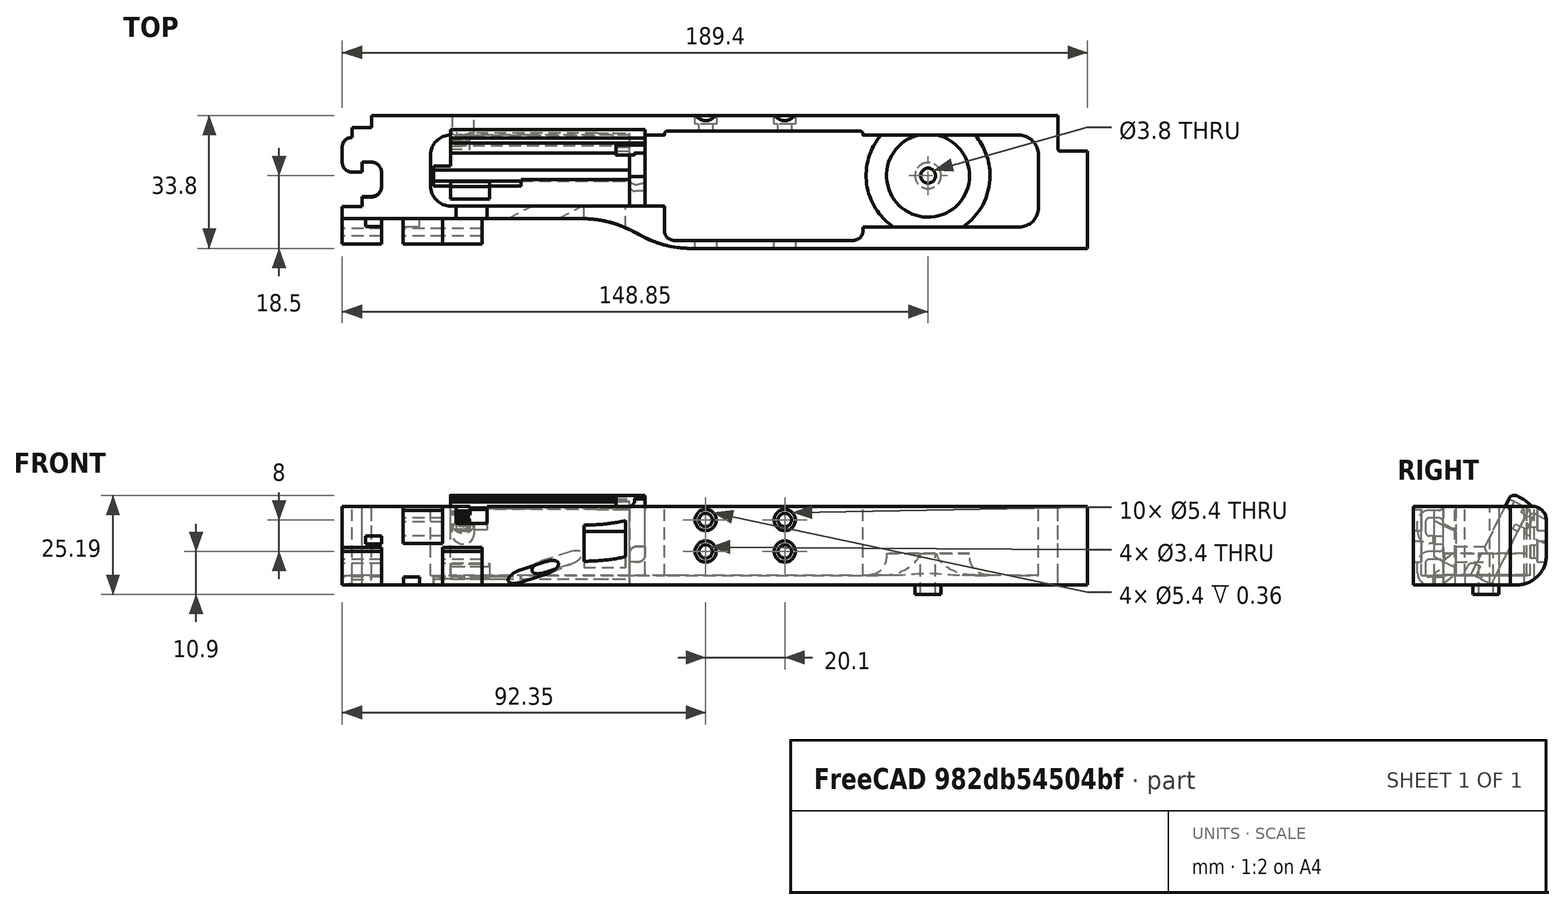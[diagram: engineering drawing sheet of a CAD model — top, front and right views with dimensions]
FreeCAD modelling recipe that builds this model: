
FCSTD DOCUMENT  (FreeCAD 0.19R0.19.2)
Label: v0_9995
License: All rights reserved
LicenseURL: http://en.wikipedia.org/wiki/All_rights_reserved
objects: Sketcher::SketchObject×44, Part::Extrusion×35, Part::MultiFuse×23, Part::Box×18, Part::Cut×15, Part::Fillet×13, App::MeasureDistance×10, Part::Cylinder×4, Part::Revolution×1, Mesh::Feature×1
note: 153 computed .brp shape members not serialized (recipe doc carries the construction recipe); baked Part::Feature solids carry a one-line shape summary decoded from their .brp

FEATURE [Sketcher::SketchObject] Sketch
  FullyConstrained = true
  sketch-geometry (36):
    g0: LineSegment StartX=0 StartY=0 StartZ=0 EndX=154.4 EndY=0 EndZ=0
    g1: LineSegment StartX=154.4 StartY=0 StartZ=0 EndX=154.4 EndY=-7.6 EndZ=0
    g2: LineSegment StartX=32.5209 StartY=-26.2 StartZ=0 EndX=-7.5 EndY=-26.2 EndZ=0
    g3-g7: Circle x5 (B-spline internal-alignment scaffolding for g8; pole/knot coordinates omitted)
    g8: BSplineCurve PolesCount=5 KnotsCount=3 Degree=3 IsPeriodic=0
    g9: GeomPoint X=61.85 Y=-33.8 Z=0
    g10: GeomPoint X=47.185 Y=-29.9 Z=0
    g11: GeomPoint X=32.5209 Y=-26.2 Z=0
    g12: Circle CenterX=121.35 CenterY=-14.3 CenterZ=0 NormalX=0 NormalY=0 NormalZ=1 AngleXU=0 Radius=3.25
    g13: LineSegment StartX=-7.5 StartY=-26.2 StartZ=0 EndX=-27.5 EndY=-26.2 EndZ=0
    g14: LineSegment StartX=-20 StartY=0 StartZ=0 EndX=0 EndY=0 EndZ=0
    g15: LineSegment StartX=-25 StartY=-3.1 StartZ=0 EndX=-20 EndY=-3.1 EndZ=0
    g16: LineSegment StartX=-25 StartY=-3.1 StartZ=0 EndX=-25 EndY=-5.6 EndZ=0
    g17: LineSegment StartX=-27.5 StartY=-8.1 StartZ=0 EndX=-27.5 EndY=-11.85 EndZ=0
    g18: ArcOfCircle CenterX=-25 CenterY=-8.1 CenterZ=0 NormalX=0 NormalY=0 NormalZ=1 AngleXU=0 Radius=2.5 StartAngle=1.5708 EndAngle=3.14159
    g19: LineSegment StartX=-25 StartY=-14.35 StartZ=0 EndX=-22.5 EndY=-14.35 EndZ=0
    g20: ArcOfCircle CenterX=-25 CenterY=-11.85 CenterZ=0 NormalX=0 NormalY=0 NormalZ=1 AngleXU=0 Radius=2.5 StartAngle=3.14159 EndAngle=4.71239
    g21: LineSegment StartX=-22.5 StartY=-14.35 StartZ=0 EndX=-22.5 EndY=-11.85 EndZ=0
    g22: LineSegment StartX=-22.5 StartY=-11.85 StartZ=0 EndX=-20 EndY=-11.85 EndZ=0
    g23: ArcOfCircle CenterX=-20 CenterY=-14.35 CenterZ=0 NormalX=0 NormalY=0 NormalZ=1 AngleXU=0 Radius=2.5 StartAngle=8e-16 EndAngle=1.5708
    g24: LineSegment StartX=-17.5 StartY=-14.35 StartZ=0 EndX=-17.5 EndY=-18.1 EndZ=0
    g25: ArcOfCircle CenterX=-20 CenterY=-18.1 CenterZ=0 NormalX=0 NormalY=0 NormalZ=1 AngleXU=0 Radius=2.5 StartAngle=4.71239 EndAngle=6.28319
    g26: LineSegment StartX=-22.5 StartY=-20.6 StartZ=0 EndX=-20 EndY=-20.6 EndZ=0
    g27: LineSegment StartX=-22.5 StartY=-20.6 StartZ=0 EndX=-22.5 EndY=-23.1 EndZ=0
    g28: LineSegment StartX=-27.5 StartY=-23.1 StartZ=0 EndX=-22.5 EndY=-23.1 EndZ=0
    g29: LineSegment StartX=-20 StartY=-3.1 StartZ=0 EndX=-20 EndY=0 EndZ=0
    g30: LineSegment StartX=-27.5 StartY=-23.1 StartZ=0 EndX=-27.5 EndY=-26.2 EndZ=0
    g31: LineSegment StartX=154.4 StartY=-7.6 StartZ=0 EndX=154.4 EndY=-8.6 EndZ=0
    g32: ArcOfCircle CenterX=154.9 CenterY=-8.6 CenterZ=0 NormalX=0 NormalY=0 NormalZ=1 AngleXU=0 Radius=0.5 StartAngle=3.14159 EndAngle=4.71239
    g33: LineSegment StartX=154.9 StartY=-9.1 StartZ=0 EndX=161.9 EndY=-9.1 EndZ=0
    g34: LineSegment StartX=161.9 StartY=-9.1 StartZ=0 EndX=161.9 EndY=-33.8 EndZ=0
    g35: LineSegment StartX=161.9 StartY=-33.8 StartZ=0 EndX=61.85 EndY=-33.8 EndZ=0
  constraints (72):
    c: PointOnObject(g0,g-2)
    c: Horizontal(g0)
    c: Distance(g0) = 154.4
    c: DistanceY(g-1,g0) = 0
    c: Vertical(g1)
    c: Distance(g1) = 7.6
    c: Coincident(g1,g0)
    c: Horizontal(g2)
    c: Block(g2)
    c: Weight(g3) = 1
    c: Coincident(g8,g2)
    c: InternalAlignment(g3-g7 -> g8) x5
    c: InternalAlignment(g9,g8)
    c: InternalAlignment(g10,g8)
    c: InternalAlignment(g11,g8)
    c: Block(g12)
    c: Coincident(g13,g2)
    c: Horizontal(g13)
    c: Distance(g13) = 20
    c: Horizontal(g14)
    c: Distance(g14) = 20
    c: Coincident(g14,g0)
    c: Horizontal(g15)
    c: Vertical(g16)
    c: Coincident(g16,g15)
    c: Vertical(g17)
    c: Coincident(g18,g16)
    c: Block(g18)
    c: Coincident(g17,g18)
    c: Horizontal(g19)
    c: Coincident(g20,g17)
    c: Block(g20)
    c: Block(g19)
    c: Vertical(g21)
    c: Coincident(g21,g19)
    c: Horizontal(g22)
    c: Coincident(g22,g21)
    c: Coincident(g23,g22)
    c: Vertical(g24)
    c: Block(g23)
    c: Coincident(g24,g23)
    c: Coincident(g25,g24)
    c: Block(g25)
    c: Horizontal(g26)
    c: Coincident(g26,g25)
    c: Vertical(g27)
    c: Coincident(g27,g26)
    c: Horizontal(g28)
    c: Coincident(g28,g27)
    c: Block(g15)
    c: Block(g28)
    c: Coincident(g29,g15)
    c: Coincident(g29,g14)
    c: Vertical(g29)
    c: Coincident(g30,g28)
    c: Coincident(g30,g13)
    c: Vertical(g30)
    c: Vertical(g31)
    c: Distance(g31) = 1
    c: Coincident(g31,g1)
    c: Coincident(g32,g31)
    c: Block(g32)
    c: Coincident(g33,g32)
    c: Horizontal(g33)
    c: Coincident(g34,g33)
    c: Vertical(g34)
    c: Block(g34)
    c: Coincident(g35,g34)
    c: Horizontal(g35)
    c: Block(g35)
    c: Coincident(g8,g35)
    c: Block(g8)
FEATURE [Part::Extrusion] Extrude  label="mainBodyBaseExtrude"
  Base = -> Sketch
  Dir = (0,0,1)
  DirMode = 2
  FaceMakerClass = Part::FaceMakerBullseye
  LengthFwd = 2.4
  LengthRev = 0
  Solid = true
  Symmetric = false
FEATURE [Sketcher::SketchObject] Sketch001
  FullyConstrained = true
  sketch-geometry (75):
    g0: ArcOfCircle CenterX=144.4 CenterY=-10 CenterZ=0 NormalX=0 NormalY=0 NormalZ=1 AngleXU=0 Radius=5 StartAngle=4.345e-13 EndAngle=1.5708
    g1: LineSegment StartX=32.5209 StartY=-26.2 StartZ=0 EndX=-7.49911 EndY=-26.2 EndZ=0
    g2: LineSegment StartX=0 StartY=0 StartZ=0 EndX=154.4 EndY=0 EndZ=0
    g3-g7: Circle x5 (B-spline internal-alignment scaffolding for g8; pole/knot coordinates omitted)
    g8: BSplineCurve PolesCount=5 KnotsCount=3 Degree=3 IsPeriodic=0
    g9: GeomPoint X=61.85 Y=-33.8 Z=0
    g10: GeomPoint X=47.1857 Y=-29.9 Z=0
    g11: GeomPoint X=32.5209 Y=-26.2 Z=0
    g12: LineSegment StartX=154.4 StartY=0 StartZ=0 EndX=154.4 EndY=-7.6 EndZ=0
    g13: LineSegment StartX=20 StartY=-5 StartZ=0 EndX=54.35 EndY=-5 EndZ=0
    g14: LineSegment StartX=104.85 StartY=-5 StartZ=0 EndX=144.4 EndY=-5 EndZ=0
    g15: LineSegment StartX=54.35 StartY=-23 StartZ=0 EndX=20 EndY=-23 EndZ=0
    g16: LineSegment StartX=-27.4991 StartY=-26.2 StartZ=0 EndX=-7.49911 EndY=-26.2 EndZ=0
    g17: LineSegment StartX=-20 StartY=0 StartZ=0 EndX=0 EndY=0 EndZ=0
    g18: LineSegment StartX=-27.4991 StartY=-23.2 StartZ=0 EndX=-22.5 EndY=-23.2 EndZ=0
    g19: LineSegment StartX=-22.5 StartY=-20.7 StartZ=0 EndX=-22.5 EndY=-23.2 EndZ=0
    g20: LineSegment StartX=-22.5 StartY=-20.7 StartZ=0 EndX=-20 EndY=-20.7 EndZ=0
    g21: ArcOfCircle CenterX=-20 CenterY=-18.2 CenterZ=0 NormalX=0 NormalY=0 NormalZ=1 AngleXU=0 Radius=2.5 StartAngle=4.71239 EndAngle=6.28319
    g22: LineSegment StartX=-17.5 StartY=-14.4 StartZ=0 EndX=-17.5 EndY=-18.2 EndZ=0
    g23: ArcOfCircle CenterX=-20 CenterY=-14.4 CenterZ=0 NormalX=0 NormalY=0 NormalZ=1 AngleXU=0 Radius=2.5 StartAngle=9e-16 EndAngle=1.5708
    g24: LineSegment StartX=-22.5 StartY=-11.9 StartZ=0 EndX=-20 EndY=-11.9 EndZ=0
    g25: LineSegment StartX=-22.5 StartY=-14.4 StartZ=0 EndX=-22.5 EndY=-11.9 EndZ=0
    g26: LineSegment StartX=-25 StartY=-14.4 StartZ=0 EndX=-22.5 EndY=-14.4 EndZ=0
    g27: ArcOfCircle CenterX=-25 CenterY=-11.9 CenterZ=0 NormalX=0 NormalY=0 NormalZ=1 AngleXU=0 Radius=2.5 StartAngle=3.14159 EndAngle=4.71239
    g28: LineSegment StartX=-27.5 StartY=-8.1 StartZ=0 EndX=-27.5 EndY=-11.9 EndZ=0
    g29: ArcOfCircle CenterX=-25 CenterY=-8.1 CenterZ=0 NormalX=0 NormalY=0 NormalZ=1 AngleXU=0 Radius=2.5 StartAngle=1.5708 EndAngle=3.14159
    g30: LineSegment StartX=-25 StartY=-3.1 StartZ=0 EndX=-25 EndY=-5.6 EndZ=0
    g31: LineSegment StartX=-20 StartY=-3.1 StartZ=0 EndX=-25 EndY=-3.1 EndZ=0
    g32: LineSegment StartX=-20 StartY=0 StartZ=0 EndX=-20 EndY=-3.1 EndZ=0
    g33: LineSegment StartX=-27.4991 StartY=-26.2 StartZ=0 EndX=-27.4991 EndY=-23.2 EndZ=0
    g34: LineSegment StartX=4.09e-14 StartY=-5 StartZ=0 EndX=20 EndY=-5 EndZ=0
    g35: ArcOfCircle CenterX=7.1e-15 CenterY=-18 CenterZ=0 NormalX=0 NormalY=0 NormalZ=1 AngleXU=0 Radius=5 StartAngle=3.14159 EndAngle=4.71239
    g36: ArcOfCircle CenterX=4.26e-14 CenterY=-10 CenterZ=0 NormalX=0 NormalY=0 NormalZ=1 AngleXU=0 Radius=5 StartAngle=1.5708 EndAngle=3.14159
    g37: LineSegment StartX=-5 StartY=-18 StartZ=0 EndX=-5 EndY=-10 EndZ=0
    g38: LineSegment StartX=6.2e-15 StartY=-23 StartZ=0 EndX=20 EndY=-23 EndZ=0
    g39: LineSegment StartX=154.4 StartY=-7.6 StartZ=0 EndX=154.4 EndY=-8.6 EndZ=0
    g40: LineSegment StartX=154.9 StartY=-9.1 StartZ=0 EndX=161.9 EndY=-9.1 EndZ=0
    g41: ArcOfCircle CenterX=154.9 CenterY=-8.6 CenterZ=0 NormalX=0 NormalY=0 NormalZ=1 AngleXU=0 Radius=0.5 StartAngle=3.14159 EndAngle=4.71299
    g42: LineSegment StartX=104.85 StartY=-28.3916 StartZ=0 EndX=144.408 EndY=-28.3916 EndZ=0
    g43: LineSegment StartX=149.4 StartY=-10 StartZ=0 EndX=149.4 EndY=-23.4 EndZ=0
    g44: ArcOfCircle CenterX=144.408 CenterY=-23.4 CenterZ=0 NormalX=0 NormalY=0 NormalZ=1 AngleXU=0 Radius=4.99164 StartAngle=4.71239 EndAngle=6.28319
    g45: LineSegment StartX=104.85 StartY=-28.3916 StartZ=0 EndX=104.85 EndY=-28.7833 EndZ=0
    g46: LineSegment StartX=54.35 StartY=-28.7916 StartZ=0 EndX=54.35 EndY=-23 EndZ=0
    g47: LineSegment StartX=161.9 StartY=-33.8 StartZ=0 EndX=161.9 EndY=-9.1 EndZ=0
    g48: LineSegment StartX=61.85 StartY=-33.8 StartZ=0 EndX=161.9 EndY=-33.8 EndZ=0
    g49: Circle CenterX=54.35 CenterY=-28.7916 CenterZ=0 NormalX=0 NormalY=0 NormalZ=1 AngleXU=0 Radius=1
    g50: Circle CenterX=54.35 CenterY=-31.7916 CenterZ=0 NormalX=0 NormalY=0 NormalZ=1 AngleXU=0 Radius=1
    g51: Circle CenterX=57.35 CenterY=-31.7916 CenterZ=0 NormalX=0 NormalY=0 NormalZ=1 AngleXU=0 Radius=1
    g52: BSplineCurve PolesCount=3 KnotsCount=2 Degree=2 IsPeriodic=0
    g53: GeomPoint X=54.35 Y=-28.7916 Z=0
    g54: GeomPoint X=57.35 Y=-31.7916 Z=0
    g55: Circle CenterX=104.85 CenterY=-28.7833 CenterZ=0 NormalX=0 NormalY=0 NormalZ=1 AngleXU=0 Radius=1
    g56: Circle CenterX=104.85 CenterY=-31.7916 CenterZ=0 NormalX=0 NormalY=0 NormalZ=1 AngleXU=0 Radius=1
    g57: Circle CenterX=101.85 CenterY=-31.7916 CenterZ=0 NormalX=0 NormalY=0 NormalZ=1 AngleXU=0 Radius=1
    g58: BSplineCurve PolesCount=3 KnotsCount=2 Degree=2 IsPeriodic=0
    g59: GeomPoint X=104.85 Y=-28.7833 Z=0
    g60: GeomPoint X=101.85 Y=-31.7916 Z=0
    g61: LineSegment StartX=57.35 StartY=-31.7916 StartZ=0 EndX=101.85 EndY=-31.7916 EndZ=0
    g62: Circle CenterX=54.35 CenterY=-5 CenterZ=0 NormalX=0 NormalY=0 NormalZ=1 AngleXU=0 Radius=1
    g63: Circle CenterX=54.35 CenterY=-4 CenterZ=0 NormalX=0 NormalY=0 NormalZ=1 AngleXU=0 Radius=1
    g64: Circle CenterX=55.15 CenterY=-4 CenterZ=0 NormalX=0 NormalY=0 NormalZ=1 AngleXU=0 Radius=1
    g65: BSplineCurve PolesCount=3 KnotsCount=2 Degree=2 IsPeriodic=0
    g66: GeomPoint X=54.35 Y=-5 Z=0
    g67: GeomPoint X=55.15 Y=-4 Z=0
    g68: Circle CenterX=104.85 CenterY=-5 CenterZ=0 NormalX=0 NormalY=0 NormalZ=1 AngleXU=0 Radius=1
    g69: Circle CenterX=104.85 CenterY=-4 CenterZ=0 NormalX=0 NormalY=0 NormalZ=1 AngleXU=0 Radius=1
    g70: Circle CenterX=104.05 CenterY=-4 CenterZ=0 NormalX=0 NormalY=0 NormalZ=1 AngleXU=0 Radius=1
    g71: BSplineCurve PolesCount=3 KnotsCount=2 Degree=2 IsPeriodic=0
    g72: GeomPoint X=104.85 Y=-5 Z=0
    g73: GeomPoint X=104.05 Y=-4 Z=0
    g74: LineSegment StartX=104.05 StartY=-4 StartZ=0 EndX=55.15 EndY=-4 EndZ=0
  constraints (156):
    c: PointOnObject(g2,g-2)
    c: DistanceY(g-1,g2) = 0
    c: Block(g0)
    c: Horizontal(g1)
    c: Distance(g1) = 40.02
    c: Horizontal(g2)
    c: Block(g2)
    c: Weight(g3) = 1
    c: Equal(g3, g4-g7) x4
    c: Coincident(g8,g1)
    c: InternalAlignment(g3-g7 -> g8) x5
    c: InternalAlignment(g9,g8)
    c: InternalAlignment(g10,g8)
    c: InternalAlignment(g11,g8)
    c: Vertical(g12)
    c: Coincident(g12,g2)
    c: Distance(g12) = 7.6
    c: Block(g12)
    c: Horizontal(g13)
    c: Coincident(g14,g0)
    c: Horizontal(g14)
    c: Horizontal(g15)
    c: Horizontal(g16)
    c: Distance(g16) = 20
    c: Coincident(g1,g16)
    c: Horizontal(g17)
    c: Distance(g17) = 20
    c: Coincident(g17,g2)
    c: Horizontal(g31)
    c: Vertical(g30)
    c: Coincident(g29,g30)
    c: Vertical(g28)
    c: Block(g29)
    c: Coincident(g27,g28)
    c: Block(g27)
    c: Horizontal(g26)
    c: Coincident(g26,g27)
    c: Vertical(g25)
    c: Coincident(g25,g26)
    c: Horizontal(g24)
    c: Coincident(g23,g24)
    c: Block(g23)
    c: Vertical(g22)
    c: Coincident(g21,g22)
    c: Block(g21)
    c: Horizontal(g20)
    c: Coincident(g20,g21)
    c: Vertical(g19)
    c: Coincident(g19,g20)
    c: Horizontal(g18)
    c: Coincident(g18,g19)
    c: Coincident(g32,g17)
    c: Coincident(g32,g31)
    c: Vertical(g32)
    c: Coincident(g33,g16)
    c: Coincident(g33,g18)
    c: Vertical(g33)
    c: Block(g33)
    c: Block(g18)
    c: Block(g22)
    c: Block(g26)
    c: Block(g25)
    c: Block(g24)
    c: Block(g28)
    c: Block(g31)
    c: Block(g30)
    c: Horizontal(g34)
    c: Distance(g34) = 20
    c: Block(g35)
    c: Block(g36)
    c: Coincident(g37,g35)
    c: Coincident(g37,g36)
    c: Vertical(g37)
    c: Coincident(g38,g35)
    c: Coincident(g38,g15)
    c: Horizontal(g38)
    c: Block(g38)
    c: Block(g34)
    c: Block(g13)
    c: Vertical(g39)
    c: Distance(g39) = 1
    c: Coincident(g39,g12)
    c: Horizontal(g40)
    c: Coincident(g41,g39)
    c: Coincident(g41,g40)
    c: Block(g39)
    c: Block(g41)
    c: Horizontal(g42)
    c: Vertical(g43)
    c: Distance(g43) = 13.4
    c: Coincident(g43,g0)
    c: Block(g42)
    c: Block(g43)
    c: Coincident(g44,g43)
    c: Coincident(g44,g42)
    c: Block(g44)
    c: Distance(g15) = 34.35
    c: Coincident(g45,g42)
    c: Vertical(g45)
    c: Coincident(g46,g15)
    c: Vertical(g46)
    c: Coincident(g47,g40)
    c: Vertical(g47)
    c: Block(g47)
    c: Coincident(g48,g47)
    c: Horizontal(g48)
    c: Block(g48)
    c: Coincident(g8,g48)
    c: Block(g8)
    c: Coincident(g52,g46)
    c: Weight(g49) = 1
    c: Equal(g49,g50)
    c: Equal(g49,g51)
    c: InternalAlignment(g49,g52)
    c: InternalAlignment(g50,g52)
    c: InternalAlignment(g51,g52)
    c: InternalAlignment(g53,g52)
    c: InternalAlignment(g54,g52)
    c: Coincident(g58,g45)
    c: Weight(g55) = 1
    c: Equal(g55,g56)
    c: Equal(g55,g57)
    c: InternalAlignment(g55,g58)
    c: InternalAlignment(g56,g58)
    c: InternalAlignment(g57,g58)
    c: InternalAlignment(g59,g58)
    c: InternalAlignment(g60,g58)
    c: Block(g58)
    c: Block(g52)
    c: Coincident(g61,g52)
    c: Coincident(g61,g58)
    c: Horizontal(g61)
    c: Block(g14)
    c: Coincident(g65,g13)
    c: Weight(g62) = 1
    c: Equal(g62,g63)
    c: Equal(g62,g64)
    c: InternalAlignment(g62,g65)
    c: InternalAlignment(g63,g65)
    c: InternalAlignment(g64,g65)
    c: InternalAlignment(g66,g65)
    c: InternalAlignment(g67,g65)
    c: Block(g65)
    c: Coincident(g71,g14)
    c: Weight(g68) = 1
    c: Equal(g68,g69)
    c: Equal(g68,g70)
    c: InternalAlignment(g68,g71)
    c: InternalAlignment(g69,g71)
    c: InternalAlignment(g70,g71)
    c: InternalAlignment(g72,g71)
    c: InternalAlignment(g73,g71)
    c: Block(g71)
    c: Coincident(g74,g71)
    c: Coincident(g74,g65)
    c: Horizontal(g74)
FEATURE [Sketcher::SketchObject] Sketch005
  FullyConstrained = true
  Placement = pos=(0,0,0) rot=(1,0,0;1.5708rad)
  sketch-geometry (4):
    g0: Circle CenterX=84.95 CenterY=16.5 CenterZ=0 NormalX=0 NormalY=0 NormalZ=1 AngleXU=0 Radius=1.7
    g1: Circle CenterX=84.95 CenterY=8.5 CenterZ=0 NormalX=0 NormalY=0 NormalZ=1 AngleXU=0 Radius=1.7
    g2: Circle CenterX=64.85 CenterY=8.5 CenterZ=0 NormalX=0 NormalY=0 NormalZ=1 AngleXU=0 Radius=1.7
    g3: Circle CenterX=64.85 CenterY=16.5 CenterZ=0 NormalX=0 NormalY=0 NormalZ=1 AngleXU=0 Radius=1.7
  constraints (4):
    c: Block(g0)
    c: Block(g1)
    c: Block(g2)
    c: Block(g3)
FEATURE [Part::Extrusion] Extrude004  label="removeFromMainBodyToCreateScrewHolesForSolenoidExtrude004"
  Base = -> Sketch005
  Dir = (0,-1,1.1e-15)
  DirMode = 2
  FaceMakerClass = Part::FaceMakerBullseye
  LengthFwd = 10
  LengthRev = 0
  Solid = true
  Symmetric = false
FEATURE [Sketcher::SketchObject] Sketch004
  FullyConstrained = true
  Placement = pos=(0,0,0) rot=(1,0,0;1.5708rad)
  sketch-geometry (12):
    g0: LineSegment StartX=15.75 StartY=2.5 StartZ=0 EndX=15.75 EndY=0 EndZ=0
    g1: Circle CenterX=15.75 CenterY=2.5 CenterZ=0 NormalX=0 NormalY=0 NormalZ=1 AngleXU=0 Radius=1
    g2: Circle CenterX=10.55 CenterY=2.5 CenterZ=0 NormalX=0 NormalY=0 NormalZ=1 AngleXU=0 Radius=1
    g3: Circle CenterX=10.55 CenterY=8 CenterZ=0 NormalX=0 NormalY=0 NormalZ=1 AngleXU=0 Radius=1
    g4: BSplineCurve PolesCount=3 KnotsCount=2 Degree=2 IsPeriodic=0
    g5: GeomPoint X=15.75 Y=2.5 Z=0
    g6: GeomPoint X=10.55 Y=8 Z=0
    g7: LineSegment StartX=1.9 StartY=8 StartZ=0 EndX=10.55 EndY=8 EndZ=0
    g8: LineSegment StartX=1.9 StartY=-2.4 StartZ=0 EndX=1.9 EndY=8 EndZ=0
    g9: LineSegment StartX=3.30092 StartY=-2.4 StartZ=0 EndX=3.30092 EndY=0 EndZ=0
    g10: LineSegment StartX=15.75 StartY=0 StartZ=0 EndX=3.30092 EndY=0 EndZ=0
    g11: LineSegment StartX=3.30092 StartY=-2.4 StartZ=0 EndX=1.9 EndY=-2.4 EndZ=0
  constraints (26):
    c: Vertical(g0)
    c: Distance(g0) = 2.5
    c: Coincident(g4,g0)
    c: Weight(g1) = 1
    c: Equal(g1,g2)
    c: Equal(g1,g3)
    c: InternalAlignment(g1,g4)
    c: InternalAlignment(g2,g4)
    c: InternalAlignment(g3,g4)
    c: InternalAlignment(g5,g4)
    c: InternalAlignment(g6,g4)
    c: Block(g4)
    c: Coincident(g7,g4)
    c: Horizontal(g7)
    c: Vertical(g8)
    c: Coincident(g8,g7)
    c: Block(g8)
    c: Vertical(g9)
    c: Coincident(g10,g0)
    c: PointOnObject(g10,g-1)
    c: Horizontal(g10)
    c: Coincident(g10,g9)
    c: Block(g9)
    c: Coincident(g11,g9)
    c: Coincident(g11,g8)
    c: Horizontal(g11)
FEATURE [Sketcher::SketchObject] Sketch007
  FullyConstrained = true
  Placement = pos=(0,-14.3,2.37) rot=(-1,0,0;2.03453rad)
  sketch-geometry (6):
    g0: LineSegment StartX=0 StartY=0 StartZ=0 EndX=45.5 EndY=0 EndZ=0
    g1: LineSegment StartX=0 StartY=0 StartZ=0 EndX=0 EndY=-21.2 EndZ=0
    g2: LineSegment StartX=45.5 StartY=0 StartZ=0 EndX=49.5 EndY=0 EndZ=0
    g3: LineSegment StartX=49.5 StartY=0 StartZ=0 EndX=49.5 EndY=-21.2 EndZ=0
    g4: LineSegment StartX=49.5 StartY=-21.2 StartZ=0 EndX=0 EndY=-21.2 EndZ=0
    g5: Circle CenterX=3.25 CenterY=-18.05 CenterZ=0 NormalX=0 NormalY=0 NormalZ=1 AngleXU=0 Radius=1.6
  constraints (15):
    c: Coincident(g0,g-1)
    c: Horizontal(g0)
    c: Distance(g0) = 45.5
    c: Coincident(g1,g0)
    c: Vertical(g1)
    c: Horizontal(g2)
    c: Distance(g2) = 4
    c: Coincident(g2,g0)
    c: Coincident(g3,g2)
    c: Vertical(g3)
    c: Block(g3)
    c: Coincident(g4,g3)
    c: Horizontal(g4)
    c: Coincident(g4,g1)
    c: Block(g5)
FEATURE [Part::Extrusion] Extrude005  label="solenoidDriverHolderExtrude005"
  Base = -> Sketch007
  Dir = (0,0.894389,-0.447291)
  DirMode = 2
  FaceMakerClass = Part::FaceMakerBullseye
  LengthFwd = 10
  LengthRev = 0
  Placement = pos=(0,0,-2) rot=(0,0,1;0rad)
  Solid = true
  Symmetric = false
FEATURE [Sketcher::SketchObject] Sketch008
  FullyConstrained = false
  Placement = pos=(0,-4.3,-2.6) rot=(-1,0,0;2.03453rad)
  sketch-geometry (1):
    g0: Circle CenterX=42.25 CenterY=-3.15 CenterZ=0 NormalX=0 NormalY=0 NormalZ=1 AngleXU=0 Radius=4.5
FEATURE [Sketcher::SketchObject] Sketch009
  FullyConstrained = true
  Placement = pos=(0,-4.3,-2.6) rot=(-1,0,0;2.03453rad)
  sketch-geometry (1):
    g0: Circle CenterX=3.25 CenterY=-18.0217 CenterZ=0 NormalX=0 NormalY=0 NormalZ=1 AngleXU=0 Radius=2.8
  constraints (1):
    c: Block(g0)
FEATURE [Sketcher::SketchObject] Sketch010
  FullyConstrained = true
  Placement = pos=(0,-14.3,2.37) rot=(-1,0,0;2.03453rad)
  sketch-geometry (1):
    g0: Circle CenterX=3.25 CenterY=-18.05 CenterZ=0 NormalX=0 NormalY=0 NormalZ=1 AngleXU=0 Radius=1.6
  constraints (1):
    c: Block(g0)
FEATURE [Part::Extrusion] Extrude008  label="removeFromScrewHole3"
  Base = -> Sketch010
  Dir = (0,0.894389,-0.447291)
  DirMode = 2
  FaceMakerClass = Part::FaceMakerBullseye
  LengthFwd = -25
  LengthRev = 0
  Placement = pos=(0,4,-4) rot=(0,0,1;0rad)
  Solid = true
  Symmetric = false
FEATURE [Sketcher::SketchObject] Sketch011
  FullyConstrained = true
  Placement = pos=(0,-14.3,2.37) rot=(-1,0,0;2.03453rad)
  sketch-geometry (4):
    g0: LineSegment StartX=49.5 StartY=-21.2 StartZ=0 EndX=49.5 EndY=-22.8 EndZ=0
    g1: LineSegment StartX=49.5 StartY=-22.8 StartZ=0 EndX=0.002238 EndY=-22.8 EndZ=0
    g2: LineSegment StartX=0.002238 StartY=-21.2 StartZ=0 EndX=0.002238 EndY=-22.8 EndZ=0
    g3: LineSegment StartX=49.5 StartY=-21.2 StartZ=0 EndX=0.002238 EndY=-21.2 EndZ=0
  constraints (10):
    c: Vertical(g0)
    c: Distance(g0) = 1.6
    c: Coincident(g1,g0)
    c: Horizontal(g1)
    c: Vertical(g2)
    c: Coincident(g2,g1)
    c: Coincident(g3,g0)
    c: Coincident(g3,g2)
    c: Horizontal(g3)
    c: Block(g3)
FEATURE [Part::Extrusion] Extrude009  label="solenoidDriverTopLipFront"
  Base = -> Sketch011
  Dir = (0,0.894389,-0.447291)
  DirMode = 2
  FaceMakerClass = Part::FaceMakerBullseye
  LengthFwd = -2
  LengthRev = 0
  Placement = pos=(0,-2.9,-0.35) rot=(0,0,1;0rad)
  Solid = true
  Symmetric = false
FEATURE [Sketcher::SketchObject] Sketch012
  FullyConstrained = true
  Placement = pos=(0,-14.3,2.37) rot=(-1,0,0;2.03453rad)
  sketch-geometry (4):
    g0: LineSegment StartX=49.5 StartY=-21.2 StartZ=0 EndX=49.5 EndY=-22.8 EndZ=0
    g1: LineSegment StartX=49.5 StartY=-22.8 StartZ=0 EndX=0.002238 EndY=-22.8 EndZ=0
    g2: LineSegment StartX=0.002238 StartY=-21.2 StartZ=0 EndX=0.002238 EndY=-22.8 EndZ=0
    g3: LineSegment StartX=49.5 StartY=-21.2 StartZ=0 EndX=0.002238 EndY=-21.2 EndZ=0
  constraints (10):
    c: Vertical(g0)
    c: Distance(g0) = 1.6
    c: Coincident(g1,g0)
    c: Horizontal(g1)
    c: Vertical(g2)
    c: Coincident(g2,g1)
    c: Coincident(g3,g0)
    c: Coincident(g3,g2)
    c: Horizontal(g3)
    c: Block(g3)
FEATURE [Part::Extrusion] Extrude010  label="solenoidDriverTopLipLowerExtrude010"
  Base = -> Sketch012
  Dir = (0,0.894389,-0.447291)
  DirMode = 2
  FaceMakerClass = Part::FaceMakerBullseye
  LengthFwd = 5.05
  LengthRev = 0
  Solid = true
  Symmetric = false
FEATURE [Sketcher::SketchObject] Sketch015
  FullyConstrained = true
  Placement = pos=(0,-14.3,2.37) rot=(-1,0,0;2.03453rad)
  sketch-geometry (4):
    g0: LineSegment StartX=0 StartY=1.5 StartZ=0 EndX=0 EndY=0 EndZ=0
    g1: LineSegment StartX=0 StartY=1.5 StartZ=0 EndX=5 EndY=1.5 EndZ=0
    g2: LineSegment StartX=5 StartY=1.5 StartZ=0 EndX=5 EndY=0 EndZ=0
    g3: LineSegment StartX=0 StartY=0 StartZ=0 EndX=5 EndY=0 EndZ=0
  constraints (13):
    c: Vertical(g0)
    c: Distance(g0) = 1.5
    c: Horizontal(g1)
    c: Distance(g1) = 5
    c: Coincident(g1,g0)
    c: Vertical(g2)
    c: Distance(g2) = 1.5
    c: Coincident(g2,g1)
    c: Block(g1)
    c: Block(g2)
    c: Block(g0)
    c: Coincident(g3,g0)
    c: Coincident(g3,g2)
FEATURE [Part::Extrusion] Extrude013  label="solenoidDriverBottomLipTopExtrude012"
  Base = -> Sketch015
  Dir = (0,0.894389,-0.447291)
  DirMode = 2
  FaceMakerClass = Part::FaceMakerBullseye
  LengthFwd = -6.5
  LengthRev = 0
  Placement = pos=(0,-14.15,19.65) rot=(1,0,0;1.5708rad)
  Solid = true
  Symmetric = false
FEATURE [Sketcher::SketchObject] Sketch016
  FullyConstrained = true
  Placement = pos=(0,0,0) rot=(1,0,0;1.5708rad)
  sketch-geometry (4):
    g0: Circle CenterX=84.15 CenterY=16.5 CenterZ=0 NormalX=0 NormalY=0 NormalZ=1 AngleXU=0 Radius=2.7
    g1: Circle CenterX=64.05 CenterY=16.5 CenterZ=0 NormalX=0 NormalY=0 NormalZ=1 AngleXU=0 Radius=2.7
    g2: Circle CenterX=64.05 CenterY=8.5 CenterZ=0 NormalX=0 NormalY=0 NormalZ=1 AngleXU=0 Radius=2.7
    g3: Circle CenterX=84.15 CenterY=8.5 CenterZ=0 NormalX=0 NormalY=0 NormalZ=1 AngleXU=0 Radius=2.7
  constraints (4):
    c: Block(g0)
    c: Block(g1)
    c: Block(g3)
    c: Block(g2)
FEATURE [Part::Extrusion] Extrude014  label="removeFromMainBodyToCreateScrewHoleCounterSinks"
  Base = -> Sketch016
  Dir = (0,-1,1.1e-15)
  DirMode = 2
  FaceMakerClass = Part::FaceMakerBullseye
  LengthFwd = 1.9
  LengthRev = 0
  Placement = pos=(0.8,-0.36,0) rot=(0,0,1;0rad)
  Solid = true
  Symmetric = false
FEATURE [Part::Extrusion] Extrude015  label="removeFromScrewHole2Extrude007"
  Base = -> Sketch009
  Dir = (0,0.894389,-0.447291)
  DirMode = 2
  FaceMakerClass = Part::FaceMakerBullseye
  LengthFwd = 10
  LengthRev = 0
  Placement = pos=(0,-8,2) rot=(0,0,1;0rad)
  Solid = true
  Symmetric = false
FEATURE [Sketcher::SketchObject] Sketch017
  FullyConstrained = true
  Placement = pos=(0,-14.3,2.37) rot=(-1,0,0;2.03453rad)
  sketch-geometry (4):
    g0: LineSegment StartX=0 StartY=1.5 StartZ=0 EndX=0 EndY=0 EndZ=0
    g1: LineSegment StartX=0 StartY=1.5 StartZ=0 EndX=5 EndY=1.5 EndZ=0
    g2: LineSegment StartX=5 StartY=1.5 StartZ=0 EndX=5 EndY=0 EndZ=0
    g3: LineSegment StartX=0 StartY=0 StartZ=0 EndX=5 EndY=0 EndZ=0
  constraints (13):
    c: Vertical(g0)
    c: Distance(g0) = 1.5
    c: Horizontal(g1)
    c: Distance(g1) = 5
    c: Coincident(g1,g0)
    c: Vertical(g2)
    c: Distance(g2) = 1.5
    c: Coincident(g2,g1)
    c: Block(g1)
    c: Block(g2)
    c: Block(g0)
    c: Coincident(g3,g0)
    c: Coincident(g3,g2)
FEATURE [Part::Extrusion] Extrude016  label="solenoidDriverBottomLipTopExtrude013"
  Base = -> Sketch017
  Dir = (0,0.894389,-0.447291)
  DirMode = 2
  FaceMakerClass = Part::FaceMakerBullseye
  LengthFwd = -6.5
  LengthRev = 0
  Placement = pos=(0,-15.45,20.3) rot=(1,0,0;1.5708rad)
  Solid = true
  Symmetric = false
FEATURE [Part::Fillet] Fillet005  label="solenoidDriverBottomLipTopFillet005"
  Base = -> Extrude016
  Edges = 1 edges r=1.4: [Edge6]
FEATURE [Sketcher::SketchObject] Sketch018
  FullyConstrained = true
  Placement = pos=(38.5,-14.3,2.37) rot=(-1,0,0;2.03453rad)
  sketch-geometry (4):
    g0: LineSegment StartX=11 StartY=0 StartZ=0 EndX=11 EndY=1.5 EndZ=0
    g1: LineSegment StartX=11 StartY=0 StartZ=0 EndX=3.6 EndY=0 EndZ=0
    g2: LineSegment StartX=3.6 StartY=0 StartZ=0 EndX=3.6 EndY=1.5 EndZ=0
    g3: LineSegment StartX=11 StartY=1.5 StartZ=0 EndX=3.6 EndY=1.5 EndZ=0
  constraints (12):
    c: PointOnObject(g0,g-1)
    c: Vertical(g0)
    c: Distance(g0) = 1.5
    c: Horizontal(g1)
    c: Distance(g1) = 7.4
    c: Coincident(g1,g0)
    c: Block(g0)
    c: Coincident(g2,g1)
    c: Vertical(g2)
    c: Coincident(g3,g0)
    c: Horizontal(g3)
    c: Coincident(g2,g3)
FEATURE [Part::Extrusion] Extrude017
  Base = -> Sketch018
  Dir = (0,0.894389,-0.447291)
  DirMode = 2
  FaceMakerClass = Part::FaceMakerBullseye
  LengthFwd = 4
  LengthRev = 0
  Placement = pos=(0,-8.212,34.025) rot=(1,0,0;1.5708rad)
  Solid = true
  Symmetric = false
FEATURE [Sketcher::SketchObject] Sketch019
  FullyConstrained = true
  Placement = pos=(0,0,0) rot=(1,0,0;1.5708rad)
  sketch-geometry (4):
    g0: Circle CenterX=84.95 CenterY=8.5 CenterZ=0 NormalX=0 NormalY=0 NormalZ=1 AngleXU=0 Radius=2.7
    g1: Circle CenterX=64.85 CenterY=8.5 CenterZ=0 NormalX=0 NormalY=0 NormalZ=1 AngleXU=0 Radius=2.7
    g2: Circle CenterX=64.85 CenterY=16.5 CenterZ=0 NormalX=0 NormalY=0 NormalZ=1 AngleXU=0 Radius=2.7
    g3: Circle CenterX=84.95 CenterY=16.5 CenterZ=0 NormalX=0 NormalY=0 NormalZ=1 AngleXU=0 Radius=2.7
  constraints (4):
    c: Block(g3)
    c: Block(g2)
    c: Block(g0)
    c: Block(g1)
FEATURE [Part::Extrusion] Extrude019  label="removeSolenoidAdjusterHoles"
  Base = -> Sketch019
  Dir = (0,-1,1.1e-15)
  DirMode = 2
  FaceMakerClass = Part::FaceMakerBullseye
  LengthFwd = 6
  LengthRev = 0
  Placement = pos=(0,-30,0) rot=(0,0,1;0rad)
  Solid = true
  Symmetric = false
FEATURE [Sketcher::SketchObject] Sketch020
  FullyConstrained = true
  Placement = pos=(0,-14.3,2.37) rot=(-1,0,0;2.03453rad)
  sketch-geometry (6):
    g0: LineSegment StartX=45.5 StartY=-21.2 StartZ=0 EndX=49.5 EndY=-21.2 EndZ=0
    g1: LineSegment StartX=45.5 StartY=0 StartZ=0 EndX=49.5 EndY=0 EndZ=0
    g2: LineSegment StartX=49.5 StartY=0 StartZ=0 EndX=49.5 EndY=-21.2 EndZ=0
    g3: LineSegment StartX=4 StartY=0 StartZ=0 EndX=4 EndY=-21.2 EndZ=0
    g4: LineSegment StartX=45.5 StartY=-21.2 StartZ=0 EndX=4 EndY=-21.2 EndZ=0
    g5: LineSegment StartX=4 StartY=0 StartZ=0 EndX=45.5 EndY=0 EndZ=0
  constraints (16):
    c: Horizontal(g0)
    c: Distance(g0) = 4
    c: Horizontal(g1)
    c: Distance(g1) = 4
    c: Coincident(g2,g1)
    c: Coincident(g2,g0)
    c: Vertical(g2)
    c: Block(g2)
    c: Vertical(g3)
    c: Coincident(g4,g0)
    c: Horizontal(g4)
    c: Coincident(g4,g3)
    c: Coincident(g5,g1)
    c: Horizontal(g5)
    c: Block(g3)
    c: Block(g5)
FEATURE [Part::Box] Box  label="Cube"
  AttacherType = Attacher::AttachEngine3D
  Height = 10
  Length = 190
  Placement = pos=(-30,0,0) rot=(0,0,1;0rad)
  Width = 10
FEATURE [Part::Fillet] Fillet008
  Base = -> Box
  Edges = 1 edges r=7.5: [Edge11]
FEATURE [Part::Box] Box001  label="Cube001"
  AttacherType = Attacher::AttachEngine3D
  Height = 10
  Length = 190
  Placement = pos=(-35,0,0) rot=(0,0,1;0rad)
  Width = 10
FEATURE [Part::Cut] Cut  label="filletMain"
  Base = -> Box001
  Placement = pos=(0,-10,0) rot=(0,0,1;0rad)
  Tool = -> Fillet008
FEATURE [Part::Box] Box002  label="Cube002"
  AttacherType = Attacher::AttachEngine3D
  Height = 30
  Length = 190
  Placement = pos=(-20,0,0) rot=(0,0,1;0rad)
  Width = 10
FEATURE [Part::Box] Box003  label="Cube003"
  AttacherType = Attacher::AttachEngine3D
  Height = 10
  Length = 190
  Placement = pos=(-90,-50,-10) rot=(0,0,1;0rad)
  Width = 50
FEATURE [Sketcher::SketchObject] Sketch021
  FullyConstrained = true
  Placement = pos=(0,-14.3,2.37) rot=(-1,0,0;2.03453rad)
  sketch-geometry (6):
    g0: LineSegment StartX=41.65 StartY=-3.15 StartZ=0 EndX=38.95 EndY=-3.15 EndZ=0
    g1: LineSegment StartX=36.25 StartY=-3.15 StartZ=0 EndX=38.95 EndY=-3.15 EndZ=0
    g2: LineSegment StartX=41.65 StartY=-3.15 StartZ=0 EndX=41.65 EndY=-7.15 EndZ=0
    g3: LineSegment StartX=38.95 StartY=-7.15 StartZ=0 EndX=41.65 EndY=-7.15 EndZ=0
    g4: LineSegment StartX=38.95 StartY=-7.15 StartZ=0 EndX=36.25 EndY=-7.15 EndZ=0
    g5: LineSegment StartX=36.25 StartY=-3.15 StartZ=0 EndX=36.25 EndY=-7.15 EndZ=0
  constraints (16):
    c: Horizontal(g0)
    c: Distance(g0) = 2.7
    c: Horizontal(g1)
    c: Distance(g1) = 2.7
    c: Coincident(g1,g0)
    c: Block(g0)
    c: Coincident(g2,g0)
    c: Vertical(g2)
    c: Horizontal(g3)
    c: Coincident(g3,g2)
    c: Horizontal(g4)
    c: Coincident(g5,g1)
    c: Vertical(g5)
    c: Coincident(g5,g4)
    c: Block(g3)
    c: Block(g4)
FEATURE [Sketcher::SketchObject] Sketch022
  FullyConstrained = true
  Placement = pos=(0,-14.3,2.37) rot=(-1,0,0;2.03453rad)
  sketch-geometry (6):
    g0: LineSegment StartX=41.65 StartY=-3.15 StartZ=0 EndX=38.95 EndY=-3.15 EndZ=0
    g1: LineSegment StartX=36.25 StartY=-3.15 StartZ=0 EndX=38.95 EndY=-3.15 EndZ=0
    g2: LineSegment StartX=41.65 StartY=-3.15 StartZ=0 EndX=41.65 EndY=-7.15 EndZ=0
    g3: LineSegment StartX=38.95 StartY=-7.15 StartZ=0 EndX=41.65 EndY=-7.15 EndZ=0
    g4: LineSegment StartX=38.95 StartY=-7.15 StartZ=0 EndX=36.25 EndY=-7.15 EndZ=0
    g5: LineSegment StartX=36.25 StartY=-3.15 StartZ=0 EndX=36.25 EndY=-7.15 EndZ=0
  constraints (16):
    c: Horizontal(g0)
    c: Distance(g0) = 2.7
    c: Horizontal(g1)
    c: Distance(g1) = 2.7
    c: Coincident(g1,g0)
    c: Block(g0)
    c: Coincident(g2,g0)
    c: Vertical(g2)
    c: Horizontal(g3)
    c: Coincident(g3,g2)
    c: Horizontal(g4)
    c: Coincident(g5,g1)
    c: Vertical(g5)
    c: Coincident(g5,g4)
    c: Block(g3)
    c: Block(g4)
FEATURE [Sketcher::SketchObject] Sketch024
  FullyConstrained = true
  Placement = pos=(0,-14.3,2.37) rot=(-1,0,0;2.03453rad)
  sketch-geometry (4):
    g0: LineSegment StartX=49.5 StartY=-21.2 StartZ=0 EndX=49.5 EndY=-22.8 EndZ=0
    g1: LineSegment StartX=49.5 StartY=-22.8 StartZ=0 EndX=0.002238 EndY=-22.8 EndZ=0
    g2: LineSegment StartX=0.002238 StartY=-21.2 StartZ=0 EndX=0.002238 EndY=-22.8 EndZ=0
    g3: LineSegment StartX=49.5 StartY=-21.2 StartZ=0 EndX=0.002238 EndY=-21.2 EndZ=0
  constraints (10):
    c: Vertical(g0)
    c: Distance(g0) = 1.6
    c: Coincident(g1,g0)
    c: Horizontal(g1)
    c: Vertical(g2)
    c: Coincident(g2,g1)
    c: Coincident(g3,g0)
    c: Coincident(g3,g2)
    c: Horizontal(g3)
    c: Block(g3)
FEATURE [Sketcher::SketchObject] Sketch025
  FullyConstrained = true
  Placement = pos=(0,-14.3,2.37) rot=(-1,0,0;2.03453rad)
  sketch-geometry (4):
    g0: LineSegment StartX=0 StartY=1.5 StartZ=0 EndX=0 EndY=0 EndZ=0
    g1: LineSegment StartX=0 StartY=1.5 StartZ=0 EndX=5 EndY=1.5 EndZ=0
    g2: LineSegment StartX=5 StartY=1.5 StartZ=0 EndX=5 EndY=0 EndZ=0
    g3: LineSegment StartX=0 StartY=0 StartZ=0 EndX=5 EndY=0 EndZ=0
  constraints (13):
    c: Vertical(g0)
    c: Distance(g0) = 1.5
    c: Horizontal(g1)
    c: Distance(g1) = 5
    c: Coincident(g1,g0)
    c: Vertical(g2)
    c: Distance(g2) = 1.5
    c: Coincident(g2,g1)
    c: Block(g1)
    c: Block(g2)
    c: Block(g0)
    c: Coincident(g3,g0)
    c: Coincident(g3,g2)
FEATURE [Part::Extrusion] Extrude022  label="solenoidDriverBottomLipTopExtrude014"
  Base = -> Sketch025
  Dir = (0,0.894389,-0.447291)
  DirMode = 2
  FaceMakerClass = Part::FaceMakerBullseye
  LengthFwd = -6.5
  LengthRev = 0
  Placement = pos=(0,-15.45,20.3) rot=(1,0,0;1.5708rad)
  Solid = true
  Symmetric = false
FEATURE [Part::Fillet] Fillet013  label="solenoidDriverBottomLipTopFillet006"
  Base = -> Extrude022
  Edges = 1 edges r=1.4: [Edge6]
  Placement = pos=(5,0,0) rot=(0,0,1;0rad)
FEATURE [Sketcher::SketchObject] Sketch026
  FullyConstrained = true
  Placement = pos=(0,-14.3,2.37) rot=(-1,0,0;2.03453rad)
  sketch-geometry (4):
    g0: LineSegment StartX=0 StartY=1.5 StartZ=0 EndX=0 EndY=0 EndZ=0
    g1: LineSegment StartX=0 StartY=1.5 StartZ=0 EndX=5 EndY=1.5 EndZ=0
    g2: LineSegment StartX=5 StartY=1.5 StartZ=0 EndX=5 EndY=0 EndZ=0
    g3: LineSegment StartX=0 StartY=0 StartZ=0 EndX=5 EndY=0 EndZ=0
  constraints (13):
    c: Vertical(g0)
    c: Distance(g0) = 1.5
    c: Horizontal(g1)
    c: Distance(g1) = 5
    c: Coincident(g1,g0)
    c: Vertical(g2)
    c: Distance(g2) = 1.5
    c: Coincident(g2,g1)
    c: Block(g1)
    c: Block(g2)
    c: Block(g0)
    c: Coincident(g3,g0)
    c: Coincident(g3,g2)
FEATURE [Part::Extrusion] Extrude023  label="solenoidDriverBottomLipTopExtrude015"
  Base = -> Sketch026
  Dir = (0,0.894389,-0.447291)
  DirMode = 2
  FaceMakerClass = Part::FaceMakerBullseye
  LengthFwd = -6.5
  LengthRev = 0
  Placement = pos=(5,-14.15,19.65) rot=(1,0,0;1.5708rad)
  Solid = true
  Symmetric = false
FEATURE [Sketcher::SketchObject] Sketch027
  FullyConstrained = true
  Placement = pos=(0,-14.3,2.37) rot=(-1,0,0;2.03453rad)
  sketch-geometry (5):
    g0: LineSegment StartX=45.5 StartY=-21.2 StartZ=0 EndX=49.5 EndY=-21.2 EndZ=0
    g1: LineSegment StartX=49.5 StartY=0 StartZ=0 EndX=49.5 EndY=-21.2 EndZ=0
    g2: LineSegment StartX=49.5 StartY=0 StartZ=0 EndX=49.5 EndY=1.6 EndZ=0
    g3: LineSegment StartX=45.5 StartY=-21.2 StartZ=0 EndX=45.5 EndY=1.6 EndZ=0
    g4: LineSegment StartX=49.5 StartY=1.6 StartZ=0 EndX=45.5 EndY=1.6 EndZ=0
  constraints (14):
    c: Horizontal(g0)
    c: Distance(g0) = 4
    c: Coincident(g1,g0)
    c: Vertical(g1)
    c: Block(g1)
    c: Vertical(g2)
    c: Distance(g2) = 1.6
    c: Block(g2)
    c: Coincident(g3,g0)
    c: Vertical(g3)
    c: Coincident(g4,g2)
    c: Horizontal(g4)
    c: Block(g0)
    c: Coincident(g3,g4)
FEATURE [Part::Extrusion] Extrude024
  Base = -> Sketch027
  Dir = (0,0.894389,-0.447291)
  DirMode = 2
  FaceMakerClass = Part::FaceMakerBullseye
  LengthFwd = 6.34
  LengthRev = 0
  Placement = pos=(0,-5.59,1) rot=(0,0,1;0rad)
  Solid = true
  Symmetric = false
FEATURE [Part::Fillet] Fillet014  label="solenoidDriverSideBarFillet014"
  Base = -> Extrude024
  Edges = 1 edges r=1.4: [Edge14]
  Placement = pos=(0,0.9,-0.45) rot=(0,0,1;0rad)
FEATURE [Part::Revolution] Revolve  label="mainScrewStandRevolve"
  Angle = 360
  Axis = (0,0,1)
  Base = (0,0,0)
  FaceMakerClass = Part::FaceMakerBullseye
  Placement = pos=(121.35,-15.3,0) rot=(0,0,1;0rad)
  Solid = true
  Source = -> Sketch004
  Symmetric = false
FEATURE [Part::Extrusion] Extrude021  label="solenoidDriverTopLipLowerExtrude011"
  Base = -> Sketch024
  Dir = (0,0.894389,-0.447291)
  DirMode = 2
  FaceMakerClass = Part::FaceMakerBullseye
  LengthFwd = 5.05
  LengthRev = 0
  Solid = true
  Symmetric = false
FEATURE [Part::Fillet] Fillet012  label="solenoidDriverTopLipLowerFillet004"
  Base = -> Extrude021
  Edges = 1 edges r=1.2: [Edge7]
  Placement = pos=(0,-0.9,-1.35) rot=(0,0,1;0rad)
FEATURE [Part::Fillet] Fillet003  label="solenoidDriverTopLipLowerFillet003"
  Base = -> Extrude010
  Edges = 1 edges r=1.2: [Edge7]
  Placement = pos=(0,-3,-0.3) rot=(0,0,1;0rad)
FEATURE [Part::Extrusion] Extrude025  label="mainBodyUpperExtrude025"
  Base = -> Sketch001
  Dir = (0,0,1)
  DirMode = 2
  FaceMakerClass = Part::FaceMakerBullseye
  LengthFwd = 20
  LengthRev = 0
  Solid = true
  Symmetric = false
FEATURE [Part::MultiFuse] Fusion  label="solenoidDriverBottomLipFusion"
  Placement = pos=(0,-1.6,0) rot=(0,0,1;0rad)
  Shapes = -> [Fillet005,Fillet013,Extrude023,Extrude013]
FEATURE [Sketcher::SketchObject] Sketch028
  FullyConstrained = true
  Placement = pos=(0,-14.3,2.37) rot=(-1,0,0;2.03453rad)
  sketch-geometry (4):
    g0: LineSegment StartX=0 StartY=1.5 StartZ=0 EndX=0 EndY=0 EndZ=0
    g1: LineSegment StartX=0 StartY=1.5 StartZ=0 EndX=5 EndY=1.5 EndZ=0
    g2: LineSegment StartX=5 StartY=1.5 StartZ=0 EndX=5 EndY=0 EndZ=0
    g3: LineSegment StartX=0 StartY=0 StartZ=0 EndX=5 EndY=0 EndZ=0
  constraints (13):
    c: Vertical(g0)
    c: Distance(g0) = 1.5
    c: Horizontal(g1)
    c: Distance(g1) = 5
    c: Coincident(g1,g0)
    c: Vertical(g2)
    c: Distance(g2) = 1.5
    c: Coincident(g2,g1)
    c: Block(g1)
    c: Block(g2)
    c: Block(g0)
    c: Coincident(g3,g0)
    c: Coincident(g3,g2)
FEATURE [Part::Extrusion] Extrude026  label="solenoidDriverBottomLipTopExtrude016"
  Base = -> Sketch028
  Dir = (0,0.894389,-0.447291)
  DirMode = 2
  FaceMakerClass = Part::FaceMakerBullseye
  LengthFwd = -6.5
  LengthRev = 0
  Placement = pos=(5,-14.15,19.65) rot=(1,0,0;1.5708rad)
  Solid = true
  Symmetric = false
FEATURE [Sketcher::SketchObject] Sketch029
  FullyConstrained = true
  Placement = pos=(0,-14.3,2.37) rot=(-1,0,0;2.03453rad)
  sketch-geometry (4):
    g0: LineSegment StartX=0 StartY=1.5 StartZ=0 EndX=0 EndY=0 EndZ=0
    g1: LineSegment StartX=0 StartY=1.5 StartZ=0 EndX=5 EndY=1.5 EndZ=0
    g2: LineSegment StartX=5 StartY=1.5 StartZ=0 EndX=5 EndY=0 EndZ=0
    g3: LineSegment StartX=0 StartY=0 StartZ=0 EndX=5 EndY=0 EndZ=0
  constraints (13):
    c: Vertical(g0)
    c: Distance(g0) = 1.5
    c: Horizontal(g1)
    c: Distance(g1) = 5
    c: Coincident(g1,g0)
    c: Vertical(g2)
    c: Distance(g2) = 1.5
    c: Coincident(g2,g1)
    c: Block(g1)
    c: Block(g2)
    c: Block(g0)
    c: Coincident(g3,g0)
    c: Coincident(g3,g2)
FEATURE [Part::Extrusion] Extrude027  label="solenoidDriverBottomLipTopExtrude017"
  Base = -> Sketch029
  Dir = (0,0.894389,-0.447291)
  DirMode = 2
  FaceMakerClass = Part::FaceMakerBullseye
  LengthFwd = -6.5
  LengthRev = 0
  Placement = pos=(0,-14.15,19.65) rot=(1,0,0;1.5708rad)
  Solid = true
  Symmetric = false
FEATURE [Sketcher::SketchObject] Sketch030
  FullyConstrained = true
  Placement = pos=(0,-14.3,2.37) rot=(-1,0,0;2.03453rad)
  sketch-geometry (4):
    g0: LineSegment StartX=0 StartY=1.5 StartZ=0 EndX=0 EndY=0 EndZ=0
    g1: LineSegment StartX=0 StartY=1.5 StartZ=0 EndX=5 EndY=1.5 EndZ=0
    g2: LineSegment StartX=5 StartY=1.5 StartZ=0 EndX=5 EndY=0 EndZ=0
    g3: LineSegment StartX=0 StartY=0 StartZ=0 EndX=5 EndY=0 EndZ=0
  constraints (13):
    c: Vertical(g0)
    c: Distance(g0) = 1.5
    c: Horizontal(g1)
    c: Distance(g1) = 5
    c: Coincident(g1,g0)
    c: Vertical(g2)
    c: Distance(g2) = 1.5
    c: Coincident(g2,g1)
    c: Block(g1)
    c: Block(g2)
    c: Block(g0)
    c: Coincident(g3,g0)
    c: Coincident(g3,g2)
FEATURE [Sketcher::SketchObject] Sketch031
  FullyConstrained = true
  Placement = pos=(0,-14.3,2.37) rot=(-1,0,0;2.03453rad)
  sketch-geometry (6):
    g0: LineSegment StartX=45.5 StartY=-21.2 StartZ=0 EndX=49.5 EndY=-21.2 EndZ=0
    g1: LineSegment StartX=45.5 StartY=0 StartZ=0 EndX=49.5 EndY=0 EndZ=0
    g2: LineSegment StartX=49.5 StartY=0 StartZ=0 EndX=49.5 EndY=-21.2 EndZ=0
    g3: LineSegment StartX=4 StartY=0 StartZ=0 EndX=4 EndY=-21.2 EndZ=0
    g4: LineSegment StartX=45.5 StartY=-21.2 StartZ=0 EndX=4 EndY=-21.2 EndZ=0
    g5: LineSegment StartX=4 StartY=0 StartZ=0 EndX=45.5 EndY=0 EndZ=0
  constraints (16):
    c: Horizontal(g0)
    c: Distance(g0) = 4
    c: Horizontal(g1)
    c: Distance(g1) = 4
    c: Coincident(g2,g1)
    c: Coincident(g2,g0)
    c: Vertical(g2)
    c: Block(g2)
    c: Vertical(g3)
    c: Coincident(g4,g0)
    c: Horizontal(g4)
    c: Coincident(g4,g3)
    c: Coincident(g5,g1)
    c: Horizontal(g5)
    c: Block(g3)
    c: Block(g5)
FEATURE [Part::Extrusion] Extrude028  label="removeFromSolenoidDriverMainExtrude021"
  Base = -> Sketch031
  Dir = (0,0.894389,-0.447291)
  DirMode = 2
  FaceMakerClass = Part::FaceMakerBullseye
  LengthFwd = 3.1
  LengthRev = 0
  Placement = pos=(-4,-2.42,-0.8) rot=(0,0,1;0rad)
  Solid = true
  Symmetric = false
FEATURE [Part::Extrusion] Extrude029  label="solenoidDriverBottomLipTopExtrude018"
  Base = -> Sketch030
  Dir = (0,0.894389,-0.447291)
  DirMode = 2
  FaceMakerClass = Part::FaceMakerBullseye
  LengthFwd = -6.5
  LengthRev = 0
  Placement = pos=(5,-14.15,19.65) rot=(1,0,0;1.5708rad)
  Solid = true
  Symmetric = false
FEATURE [Sketcher::SketchObject] Sketch032
  FullyConstrained = true
  Placement = pos=(0,-14.3,2.37) rot=(-1,0,0;2.03453rad)
  sketch-geometry (4):
    g0: LineSegment StartX=0 StartY=1.5 StartZ=0 EndX=0 EndY=0 EndZ=0
    g1: LineSegment StartX=0 StartY=1.5 StartZ=0 EndX=5 EndY=1.5 EndZ=0
    g2: LineSegment StartX=5 StartY=1.5 StartZ=0 EndX=5 EndY=0 EndZ=0
    g3: LineSegment StartX=0 StartY=0 StartZ=0 EndX=5 EndY=0 EndZ=0
  constraints (13):
    c: Vertical(g0)
    c: Distance(g0) = 1.5
    c: Horizontal(g1)
    c: Distance(g1) = 5
    c: Coincident(g1,g0)
    c: Vertical(g2)
    c: Distance(g2) = 1.5
    c: Coincident(g2,g1)
    c: Block(g1)
    c: Block(g2)
    c: Block(g0)
    c: Coincident(g3,g0)
    c: Coincident(g3,g2)
FEATURE [Part::Extrusion] Extrude030  label="solenoidDriverBottomLipTopExtrude019"
  Base = -> Sketch032
  Dir = (0,0.894389,-0.447291)
  DirMode = 2
  FaceMakerClass = Part::FaceMakerBullseye
  LengthFwd = -6.5
  LengthRev = 0
  Placement = pos=(0,-14.15,19.65) rot=(1,0,0;1.5708rad)
  Solid = true
  Symmetric = false
FEATURE [Part::MultiFuse] Fusion004
  Placement = pos=(0,1.4,2.65) rot=(0,0,1;0rad)
  Shapes = -> [Extrude029,Extrude030]
FEATURE [Part::MultiFuse] Fusion003
  Placement = pos=(-2.3,0,0) rot=(0,0,1;0rad)
  Shapes = -> [Extrude028,Fusion004]
FEATURE [Sketcher::SketchObject] Sketch033
  FullyConstrained = true
  Placement = pos=(0,-14.3,2.37) rot=(-1,0,0;2.03453rad)
  sketch-geometry (4):
    g0: LineSegment StartX=0 StartY=1.5 StartZ=0 EndX=0 EndY=0 EndZ=0
    g1: LineSegment StartX=0 StartY=1.5 StartZ=0 EndX=5 EndY=1.5 EndZ=0
    g2: LineSegment StartX=5 StartY=1.5 StartZ=0 EndX=5 EndY=0 EndZ=0
    g3: LineSegment StartX=0 StartY=0 StartZ=0 EndX=5 EndY=0 EndZ=0
  constraints (13):
    c: Vertical(g0)
    c: Distance(g0) = 1.5
    c: Horizontal(g1)
    c: Distance(g1) = 5
    c: Coincident(g1,g0)
    c: Vertical(g2)
    c: Distance(g2) = 1.5
    c: Coincident(g2,g1)
    c: Block(g1)
    c: Block(g2)
    c: Block(g0)
    c: Coincident(g3,g0)
    c: Coincident(g3,g2)
FEATURE [Sketcher::SketchObject] Sketch034
  FullyConstrained = true
  Placement = pos=(0,-14.3,2.37) rot=(-1,0,0;2.03453rad)
  sketch-geometry (4):
    g0: LineSegment StartX=0 StartY=1.5 StartZ=0 EndX=4 EndY=1.5 EndZ=0
    g1: LineSegment StartX=4 StartY=1.5 StartZ=0 EndX=4 EndY=-2.5 EndZ=0
    g2: LineSegment StartX=4 StartY=-2.5 StartZ=0 EndX=0 EndY=-2.5 EndZ=0
    g3: LineSegment StartX=0 StartY=1.5 StartZ=0 EndX=0 EndY=-2.5 EndZ=0
  constraints (11):
    c: Horizontal(g0)
    c: Distance(g0) = 4
    c: Block(g0)
    c: Coincident(g1,g0)
    c: Vertical(g1)
    c: Distance(g1) = 4
    c: Coincident(g2,g1)
    c: Horizontal(g2)
    c: Distance(g2) = 4
    c: Coincident(g3,g0)
    c: Coincident(g3,g2)
FEATURE [Part::Extrusion] Extrude020  label="removeFromSolenoidDriverMainExtrude020"
  Base = -> Sketch020
  Dir = (0,0.894389,-0.447291)
  DirMode = 2
  FaceMakerClass = Part::FaceMakerBullseye
  LengthFwd = 3.1
  LengthRev = 0
  Placement = pos=(-4,-2.42,-0.8) rot=(0,0,1;0rad)
  Solid = true
  Symmetric = false
FEATURE [Part::Fillet] Fillet
  Base = -> Fusion003
  Edges = 1 edges r=10: [Edge5]
  Placement = pos=(-2,0,0) rot=(0,0,1;0rad)
FEATURE [Part::MultiFuse] Fusion001
  Placement = pos=(0,1.4,2.65) rot=(0,0,1;0rad)
  Shapes = -> [Extrude026,Extrude027]
FEATURE [Part::MultiFuse] Fusion002
  Shapes = -> [Extrude020,Fusion001]
FEATURE [Sketcher::SketchObject] Sketch035
  FullyConstrained = true
  Placement = pos=(0,-14.3,2.37) rot=(-1,0,0;2.03453rad)
  sketch-geometry (4):
    g0: LineSegment StartX=0 StartY=1.5 StartZ=0 EndX=0 EndY=0 EndZ=0
    g1: LineSegment StartX=0 StartY=1.5 StartZ=0 EndX=5 EndY=1.5 EndZ=0
    g2: LineSegment StartX=5 StartY=1.5 StartZ=0 EndX=5 EndY=0 EndZ=0
    g3: LineSegment StartX=0 StartY=0 StartZ=0 EndX=5 EndY=0 EndZ=0
  constraints (13):
    c: Vertical(g0)
    c: Distance(g0) = 1.5
    c: Horizontal(g1)
    c: Distance(g1) = 5
    c: Coincident(g1,g0)
    c: Vertical(g2)
    c: Distance(g2) = 1.5
    c: Coincident(g2,g1)
    c: Block(g1)
    c: Block(g2)
    c: Block(g0)
    c: Coincident(g3,g0)
    c: Coincident(g3,g2)
FEATURE [Sketcher::SketchObject] Sketch036
  FullyConstrained = true
  Placement = pos=(0,-14.3,2.37) rot=(-1,0,0;2.03453rad)
  sketch-geometry (4):
    g0: LineSegment StartX=0 StartY=1.5 StartZ=0 EndX=0 EndY=0 EndZ=0
    g1: LineSegment StartX=0 StartY=1.5 StartZ=0 EndX=5 EndY=1.5 EndZ=0
    g2: LineSegment StartX=5 StartY=1.5 StartZ=0 EndX=5 EndY=0 EndZ=0
    g3: LineSegment StartX=0 StartY=0 StartZ=0 EndX=5 EndY=0 EndZ=0
  constraints (13):
    c: Vertical(g0)
    c: Distance(g0) = 1.5
    c: Horizontal(g1)
    c: Distance(g1) = 5
    c: Coincident(g1,g0)
    c: Vertical(g2)
    c: Distance(g2) = 1.5
    c: Coincident(g2,g1)
    c: Block(g1)
    c: Block(g2)
    c: Block(g0)
    c: Coincident(g3,g0)
    c: Coincident(g3,g2)
FEATURE [Part::Extrusion] Extrude031  label="solenoidDriverBottomLipTopExtrude020"
  Base = -> Sketch035
  Dir = (0,0.894389,-0.447291)
  DirMode = 2
  FaceMakerClass = Part::FaceMakerBullseye
  LengthFwd = -6.5
  LengthRev = 0
  Placement = pos=(5,-14.15,19.65) rot=(1,0,0;1.5708rad)
  Solid = true
  Symmetric = false
FEATURE [Part::Extrusion] Extrude032  label="solenoidDriverBottomLipTopExtrude021"
  Base = -> Sketch036
  Dir = (0,0.894389,-0.447291)
  DirMode = 2
  FaceMakerClass = Part::FaceMakerBullseye
  LengthFwd = -6.5
  LengthRev = 0
  Placement = pos=(0,-14.15,19.65) rot=(1,0,0;1.5708rad)
  Solid = true
  Symmetric = false
FEATURE [Part::MultiFuse] Fusion009
  Placement = pos=(8,1.4,2.65) rot=(0,0,1;0rad)
  Shapes = -> [Extrude031,Extrude032]
FEATURE [Part::MultiFuse] Fusion010  label="removeFromSolenoidDriver"
  Shapes = -> [Fusion009,Fillet,Fusion002]
FEATURE [Sketcher::SketchObject] Sketch037
  FullyConstrained = true
  Placement = pos=(0,0,0) rot=(1,0,0;1.5708rad)
  sketch-geometry (4):
    g0: Circle CenterX=64.05 CenterY=16.5 CenterZ=0 NormalX=0 NormalY=0 NormalZ=1 AngleXU=0 Radius=2.7
    g1: Circle CenterX=64.05 CenterY=8.5 CenterZ=0 NormalX=0 NormalY=0 NormalZ=1 AngleXU=0 Radius=2.7
    g2: Circle CenterX=84.15 CenterY=8.5 CenterZ=0 NormalX=0 NormalY=0 NormalZ=1 AngleXU=0 Radius=2.7
    g3: Circle CenterX=84.15 CenterY=16.5 CenterZ=0 NormalX=0 NormalY=0 NormalZ=1 AngleXU=0 Radius=2.7
  constraints (4):
    c: Block(g2)
    c: Block(g3)
    c: Block(g0)
    c: Block(g1)
FEATURE [Part::Extrusion] Extrude033  label="removeFromMainBodyToCreateScrewHoleCounterSinks001"
  Base = -> Sketch037
  Dir = (0,-1,1.1e-15)
  DirMode = 2
  FaceMakerClass = Part::FaceMakerBullseye
  LengthFwd = 1.9
  LengthRev = 0
  Placement = pos=(0.8,0,0) rot=(0,0,1;0rad)
  Solid = true
  Symmetric = false
FEATURE [Part::MultiFuse] Fusion011  label="removeFromMainBodyToCreateScrewHoleCounterSinks001Fusion011"
  Shapes = -> [Extrude014,Extrude033]
FEATURE [Sketcher::SketchObject] Sketch038
  FullyConstrained = true
  Placement = pos=(0,-14.3,2.37) rot=(-1,0,0;2.03453rad)
  sketch-geometry (4):
    g0: LineSegment StartX=33.9 StartY=-9.7 StartZ=0 EndX=33.9 EndY=-1.5 EndZ=0
    g1: LineSegment StartX=33.9 StartY=-1.5 StartZ=0 EndX=44.5 EndY=-1.5 EndZ=0
    g2: LineSegment StartX=33.9 StartY=-9.7 StartZ=0 EndX=44.5 EndY=-9.7 EndZ=0
    g3: LineSegment StartX=44.5 StartY=-1.5 StartZ=0 EndX=44.5 EndY=-9.7 EndZ=0
  constraints (10):
    c: Vertical(g0)
    c: Coincident(g1,g0)
    c: Horizontal(g1)
    c: Block(g1)
    c: Block(g0)
    c: Coincident(g2,g0)
    c: Horizontal(g2)
    c: Coincident(g3,g1)
    c: Coincident(g3,g2)
    c: Vertical(g3)
FEATURE [Part::Extrusion] Extrude034
  Base = -> Sketch038
  Dir = (0,0.894389,-0.447291)
  DirMode = 2
  FaceMakerClass = Part::FaceMakerBullseye
  LengthFwd = 16
  LengthRev = 0
  Placement = pos=(0,-22,7) rot=(0,0,1;0rad)
  Solid = true
  Symmetric = false
FEATURE [Sketcher::SketchObject] Sketch039
  FullyConstrained = true
  Placement = pos=(0,-14.3,2.37) rot=(-1,0,0;2.03453rad)
  sketch-geometry (4):
    g0: LineSegment StartX=5.5 StartY=-7.7 StartZ=0 EndX=13.3 EndY=-7.7 EndZ=0
    g1: LineSegment StartX=13.3 StartY=-7.7 StartZ=0 EndX=13.3 EndY=-13.1 EndZ=0
    g2: LineSegment StartX=13.3 StartY=-13.1 StartZ=0 EndX=5.5 EndY=-13.1 EndZ=0
    g3: LineSegment StartX=5.5 StartY=-7.7 StartZ=0 EndX=5.5 EndY=-13.1 EndZ=0
  constraints (12):
    c: Horizontal(g0)
    c: Distance(g0) = 7.8
    c: Coincident(g1,g0)
    c: Vertical(g1)
    c: Distance(g1) = 5.4
    c: Coincident(g2,g1)
    c: Horizontal(g2)
    c: Vertical(g3)
    c: Coincident(g3,g2)
    c: Block(g0)
    c: Block(g2)
    c: Block(g3)
FEATURE [Part::Extrusion] Extrude035  label="removeToMakeHoleForConnectorExtrude035"
  Base = -> Sketch039
  Dir = (0,0.894389,-0.447291)
  DirMode = 2
  FaceMakerClass = Part::FaceMakerBullseye
  LengthFwd = 15
  LengthRev = 0
  Placement = pos=(-4,-22,9.6469) rot=(0,0,1;0rad)
  Solid = true
  Symmetric = false
FEATURE [App::MeasureDistance] Distance  label="Distance: 4.00 mm"
  Distance = 4.00184
  P1 = (119.349,-15.3,8)
  P2 = (123.351,-15.3,8)
FEATURE [App::MeasureDistance] Distance001  label="Distance: 3.80 mm"
  Distance = 3.8
  P1 = (119.45,-15.3,8)
  P2 = (123.25,-15.3,8)
FEATURE [Part::Fillet] Fillet015
  Base = -> Extrude009
  Edges = 1 edges r=1.59: [Edge7]
FEATURE [Part::Fillet] Fillet016
  Base = -> Extrude017
  Edges = 1 edges r=1.49: [Edge12]
FEATURE [Part::Fillet] Fillet017
  Base = -> Fillet016
  Edges = 1 edges r=1.45: [Edge8]
FEATURE [Part::MultiFuse] Fusion012  label="main"
  Shapes = -> [Extrude,Revolve,Extrude005,Fillet003,Fillet012,Fillet014,Extrude025,Fusion,Fillet015,Fillet017]
FEATURE [Part::Cut] Cut001
  Base = -> Fusion012
  Tool = -> Box003
FEATURE [Part::Cut] Cut002
  Base = -> Cut001
  Tool = -> Box002
FEATURE [Part::Cut] Cut003
  Base = -> Cut002
  Tool = -> Cut
FEATURE [Part::Cut] Cut004
  Base = -> Cut003
  Tool = -> Extrude019
FEATURE [Part::Cut] Cut005
  Base = -> Cut004
  Tool = -> Fusion011
FEATURE [Part::Cut] Cut006
  Base = -> Cut005
  Tool = -> Extrude004
FEATURE [Part::Cut] Cut007
  Base = -> Cut006
  Tool = -> Extrude015
FEATURE [Part::Cut] Cut008
  Base = -> Cut007
  Tool = -> Extrude008
FEATURE [Part::Cut] Cut009
  Base = -> Cut008
  Tool = -> Fusion010
FEATURE [App::MeasureDistance] Distance002  label="Distance: 2.05 mm"
  Distance = 2.05453
  P1 = (1.5,-23.0732,21.402)
  P2 = (6e-15,-23,20)
FEATURE [Part::Cut] Cut010
  Base = -> Cut009
  Tool = -> Extrude035
FEATURE [Part::Cut] Cut011
  Base = -> Cut010
  Tool = -> Extrude034
FEATURE [Part::Box] Box004  label="Cube004"
  AttacherType = Attacher::AttachEngine3D
  Height = 10
  Length = 200
  Placement = pos=(-30,0,0) rot=(0,0,1;0rad)
  Width = 10
FEATURE [Part::Fillet] Fillet020
  Base = -> Box004
  Edges = 1 edges r=3.6: [Edge12]
FEATURE [Part::Box] Box005  label="Cube005"
  AttacherType = Attacher::AttachEngine3D
  Height = 10
  Length = 198
  Placement = pos=(-30,0,0) rot=(0,0,1;0rad)
  Width = 10
FEATURE [Part::Cut] Cut012
  Base = -> Box005
  Tool = -> Fillet020
FEATURE [Part::Box] Box006  label="Cube006"
  AttacherType = Attacher::AttachEngine3D
  Height = 5
  Length = 200
  Placement = pos=(-30,6.4,10) rot=(1,0,0;0rad)
  Width = 5
FEATURE [Part::Box] Box007  label="Cube007"
  AttacherType = Attacher::AttachEngine3D
  Height = 5
  Length = 200
  Placement = pos=(-30,6.4,10) rot=(1,0,0;0.872665rad)
  Width = 5
FEATURE [Part::MultiFuse] Fusion013  label="removeFromMainFusion013"
  Placement = pos=(0,-10,10) rot=(0,0,1;0rad)
  Shapes = -> [Box007,Box006,Cut012]
FEATURE [Mesh::Feature] v0_98_Cut013  label="v0_98-Cut013"
FEATURE [App::MeasureDistance] Distance003  label="Distance: 7.18 mm"
  Distance = 7.17719
  P1 = (117.773,-15.3145,-2.4)
  P2 = (124.951,-15.2973,-2.4)
FEATURE [Sketcher::SketchObject] Sketch040
  FullyConstrained = true
  Placement = pos=(0,-14.3,2.37) rot=(-1,0,0;2.03453rad)
  sketch-geometry (4):
    g0: LineSegment StartX=0 StartY=1.5 StartZ=0 EndX=0 EndY=0 EndZ=0
    g1: LineSegment StartX=0 StartY=1.5 StartZ=0 EndX=5 EndY=1.5 EndZ=0
    g2: LineSegment StartX=5 StartY=1.5 StartZ=0 EndX=5 EndY=0 EndZ=0
    g3: LineSegment StartX=0 StartY=0 StartZ=0 EndX=5 EndY=0 EndZ=0
  constraints (13):
    c: Vertical(g0)
    c: Distance(g0) = 1.5
    c: Horizontal(g1)
    c: Distance(g1) = 5
    c: Coincident(g1,g0)
    c: Vertical(g2)
    c: Distance(g2) = 1.5
    c: Coincident(g2,g1)
    c: Block(g1)
    c: Block(g2)
    c: Block(g0)
    c: Coincident(g3,g0)
    c: Coincident(g3,g2)
FEATURE [Part::Extrusion] Extrude036
  Base = -> Sketch040
  Dir = (0,0.894389,-0.447291)
  DirMode = 2
  FaceMakerClass = Part::FaceMakerBullseye
  LengthFwd = 1.4
  LengthRev = 0
  Placement = pos=(0,8.25,17.58) rot=(0,0,1;0rad)
  Solid = true
  Symmetric = false
FEATURE [Sketcher::SketchObject] Sketch041
  FullyConstrained = true
  Placement = pos=(0,-14.3,2.37) rot=(-1,0,0;2.03453rad)
  sketch-geometry (4):
    g0: LineSegment StartX=0 StartY=1.5 StartZ=0 EndX=0 EndY=0 EndZ=0
    g1: LineSegment StartX=0 StartY=1.5 StartZ=0 EndX=5 EndY=1.5 EndZ=0
    g2: LineSegment StartX=5 StartY=1.5 StartZ=0 EndX=5 EndY=0 EndZ=0
    g3: LineSegment StartX=0 StartY=0 StartZ=0 EndX=5 EndY=0 EndZ=0
  constraints (13):
    c: Vertical(g0)
    c: Distance(g0) = 1.5
    c: Horizontal(g1)
    c: Distance(g1) = 5
    c: Coincident(g1,g0)
    c: Vertical(g2)
    c: Distance(g2) = 1.5
    c: Coincident(g2,g1)
    c: Block(g1)
    c: Block(g2)
    c: Block(g0)
    c: Coincident(g3,g0)
    c: Coincident(g3,g2)
FEATURE [Part::Extrusion] Extrude037
  Base = -> Sketch041
  Dir = (0,0.894389,-0.447291)
  DirMode = 2
  FaceMakerClass = Part::FaceMakerBullseye
  LengthFwd = 1.4
  LengthRev = 0
  Placement = pos=(0,6.11,13.33) rot=(0,0,1;0rad)
  Solid = true
  Symmetric = false
FEATURE [Part::MultiFuse] Fusion014  label="screwSpacerFusion014"
  Shapes = -> [Extrude037,Extrude036]
FEATURE [Sketcher::SketchObject] Sketch042
  FullyConstrained = true
  Placement = pos=(0,-14.3,2.37) rot=(-1,0,0;2.03453rad)
  sketch-geometry (4):
    g0: LineSegment StartX=0 StartY=1.5 StartZ=0 EndX=0 EndY=0 EndZ=0
    g1: LineSegment StartX=0 StartY=1.5 StartZ=0 EndX=5 EndY=1.5 EndZ=0
    g2: LineSegment StartX=5 StartY=1.5 StartZ=0 EndX=5 EndY=0 EndZ=0
    g3: LineSegment StartX=0 StartY=0 StartZ=0 EndX=5 EndY=0 EndZ=0
  constraints (13):
    c: Vertical(g0)
    c: Distance(g0) = 1.5
    c: Horizontal(g1)
    c: Distance(g1) = 5
    c: Coincident(g1,g0)
    c: Vertical(g2)
    c: Distance(g2) = 1.5
    c: Coincident(g2,g1)
    c: Block(g1)
    c: Block(g2)
    c: Block(g0)
    c: Coincident(g3,g0)
    c: Coincident(g3,g2)
FEATURE [Part::Extrusion] Extrude038
  Base = -> Sketch042
  Dir = (0,0.894389,-0.447291)
  DirMode = 2
  FaceMakerClass = Part::FaceMakerBullseye
  LengthFwd = 1.4
  LengthRev = 0
  Placement = pos=(0,8.459,18) rot=(0,0,1;0rad)
  Solid = true
  Symmetric = false
FEATURE [Part::MultiFuse] Fusion015  label="screwSpacerFusion014Fusion015"
  Placement = pos=(0,0.35,-0.18) rot=(0,0,1;0rad)
  Shapes = -> [Extrude038,Fusion014]
FEATURE [Part::Cylinder] Cylinder
  Angle = 360
  AttacherType = Attacher::AttachEngine3D
  Height = 10
  Placement = pos=(0,10,0) rot=(0,0,1;0rad)
  Radius = 1.5
FEATURE [Part::Cylinder] Cylinder001
  Angle = 360
  AttacherType = Attacher::AttachEngine3D
  Height = 10
  Placement = pos=(3,10,0) rot=(0,0,1;0rad)
  Radius = 1.5
FEATURE [Part::Box] Box008  label="Cube008"
  AttacherType = Attacher::AttachEngine3D
  Height = 10
  Length = 3
  Placement = pos=(0,8.5,0) rot=(0,0,1;0rad)
  Width = 3
FEATURE [Part::MultiFuse] Fusion016  label="holeForWireFusion016"
  Shapes = -> [Cylinder001,Box008,Cylinder]
FEATURE [Part::Box] Box009  label="Cube009"
  AttacherType = Attacher::AttachEngine3D
  Height = 10
  Length = 3
  Placement = pos=(0,8.5,0) rot=(0,0,1;0rad)
  Width = 3
FEATURE [Part::Cylinder] Cylinder002
  Angle = 360
  AttacherType = Attacher::AttachEngine3D
  Height = 10
  Placement = pos=(0,10,0) rot=(0,0,1;0rad)
  Radius = 1.5
FEATURE [Part::Cylinder] Cylinder003
  Angle = 360
  AttacherType = Attacher::AttachEngine3D
  Height = 10
  Placement = pos=(3,10,0) rot=(0,0,1;0rad)
  Radius = 1.5
FEATURE [Part::MultiFuse] Fusion017  label="holeForWireFusion017"
  Placement = pos=(0,0,10) rot=(0,0,1;0rad)
  Shapes = -> [Cylinder003,Box009,Cylinder002]
FEATURE [Part::MultiFuse] Fusion018  label="holeForWireFusion018"
  Placement = pos=(0,0,0) rot=(0,1,0;-1.5708rad)
  Shapes = -> [Fusion017,Fusion016]
FEATURE [Part::Box] Box010  label="Cube010"
  AttacherType = Attacher::AttachEngine3D
  Height = 0.1
  Length = 0.1
  Placement = pos=(-2,10,0) rot=(0,0.995037,0.099504;0rad)
  Width = 0.1
FEATURE [Part::MultiFuse] Fusion019
  Placement = pos=(0,10,0) rot=(1,0,0;1.5708rad)
  Shapes = -> [Box010,Fusion018]
FEATURE [Part::Box] Box011  label="Cube011"
  AttacherType = Attacher::AttachEngine3D
  Height = 0.1
  Length = 1.1
  Placement = pos=(-2,10,10) rot=(0,0.995037,0.099504;0rad)
  Width = 0.1
FEATURE [Part::MultiFuse] Fusion020
  Placement = pos=(0,0,0) rot=(0,1,0;0.349066rad)
  Shapes = -> [Box011,Fusion019]
FEATURE [Part::Box] Box012  label="Cube012"
  AttacherType = Attacher::AttachEngine3D
  Height = 0.1
  Length = 1.1
  Placement = pos=(-2,10,10) rot=(0,0.995037,0.099504;0rad)
  Width = 0.1
FEATURE [Part::MultiFuse] Fusion021
  Placement = pos=(0,30,0) rot=(0,0,1;-2.6529rad)
  Shapes = -> [Box012,Fusion020]
FEATURE [Part::Box] Box013  label="Cube013"
  AttacherType = Attacher::AttachEngine3D
  Height = 0.1
  Length = 1.1
  Placement = pos=(2,19,10) rot=(0,0.995037,0.099504;0rad)
  Width = 0.1
FEATURE [Part::MultiFuse] Fusion022  label="holeForWire"
  Placement = pos=(15,-49.8,-8.2) rot=(0,0,1;0rad)
  Shapes = -> [Box013,Fusion021]
FEATURE [Part::Cut] Cut013
  Base = -> Cut011
  Tool = -> Fusion013
FEATURE [Part::Cut] Cut014
  Base = -> Cut013
  Tool = -> Fusion022
FEATURE [Sketcher::SketchObject] Sketch043
  FullyConstrained = true
  MapMode = 4
  Placement = pos=(0,0,0) rot=(0.57735,0.57735,0.57735;2.0944rad)
  Support = -> [Cut014]
  sketch-geometry (14):
    g0: LineSegment StartX=6.08745 StartY=-4.11588 StartZ=0 EndX=6.08745 EndY=-2.11589 EndZ=0
    g1: LineSegment StartX=3.58745 StartY=2.38411 StartZ=0 EndX=3.58745 EndY=4.38411 EndZ=0
    g2: LineSegment StartX=8.08745 StartY=1.38411 StartZ=0 EndX=8.08745 EndY=-1.11589 EndZ=0
    g3: ArcOfCircle CenterX=7.08745 CenterY=-1.11589 CenterZ=0 NormalX=0 NormalY=0 NormalZ=1 AngleXU=0 Radius=1 StartAngle=4.71239 EndAngle=6.28319
    g4: LineSegment StartX=6.08745 StartY=-2.11589 StartZ=0 EndX=7.08745 EndY=-2.11589 EndZ=0
    g5: LineSegment StartX=6.08745 StartY=-4.11588 StartZ=0 EndX=7.08745 EndY=-4.11588 EndZ=0
    g6: ArcOfCircle CenterX=7.08745 CenterY=-1.11589 CenterZ=0 NormalX=0 NormalY=0 NormalZ=1 AngleXU=0 Radius=3 StartAngle=4.71239 EndAngle=6.28319
    g7: ArcOfCircle CenterX=7.08745 CenterY=1.38411 CenterZ=0 NormalX=0 NormalY=0 NormalZ=1 AngleXU=0 Radius=1 StartAngle=5.35e-14 EndAngle=1.5708
    g8: LineSegment StartX=3.58745 StartY=4.38411 StartZ=0 EndX=7.08745 EndY=4.38411 EndZ=0
    g9: LineSegment StartX=10.0875 StartY=-1.11588 StartZ=0 EndX=10.0875 EndY=1.38411 EndZ=0
    g10: ArcOfCircle CenterX=7.08745 CenterY=1.38411 CenterZ=0 NormalX=0 NormalY=0 NormalZ=1 AngleXU=0 Radius=3 StartAngle=3.57e-14 EndAngle=1.5708
    g11: LineSegment StartX=3.58745 StartY=2.38411 StartZ=0 EndX=3.58745 EndY=1.38411 EndZ=0
    g12: ArcOfCircle CenterX=4.58745 CenterY=1.38412 CenterZ=0 NormalX=0 NormalY=0 NormalZ=1 AngleXU=0 Radius=1 StartAngle=1.57081 EndAngle=3.14159
    g13: LineSegment StartX=4.58744 StartY=2.38411 StartZ=0 EndX=7.08745 EndY=2.38411 EndZ=0
  constraints (33):
    c: Vertical(g0)
    c: Vertical(g1)
    c: Distance(g1) = 2
    c: Block(g0)
    c: Block(g2)
    c: Coincident(g3,g2)
    c: Coincident(g4,g0)
    c: Coincident(g4,g3)
    c: Horizontal(g4)
    c: Block(g3)
    c: Coincident(g5,g0)
    c: Horizontal(g5)
    c: Coincident(g6,g3)
    c: Block(g6)
    c: Block(g5)
    c: Coincident(g7,g2)
    c: Block(g7)
    c: Coincident(g8,g1)
    c: Coincident(g9,g6)
    c: Vertical(g9)
    c: Coincident(g10,g7)
    c: Block(g10)
    c: Block(g8)
    c: Block(g9)
    c: Coincident(g11,g1)
    c: Vertical(g11)
    c: Distance(g11) = 1
    c: Coincident(g12,g11)
    c: Coincident(g13,g12)
    c: Coincident(g13,g7)
    c: Horizontal(g13)
    c: Block(g13)
    c: Block(g12)
FEATURE [Sketcher::SketchObject] Sketch044
  FullyConstrained = true
  MapMode = 4
  Placement = pos=(0,0,0) rot=(0.57735,0.57735,0.57735;2.0944rad)
  Support = -> [Cut014]
  sketch-geometry (14):
    g0: LineSegment StartX=6.08745 StartY=-4.11588 StartZ=0 EndX=6.08745 EndY=-2.11589 EndZ=0
    g1: LineSegment StartX=8.08745 StartY=1.38411 StartZ=0 EndX=8.08745 EndY=-1.11589 EndZ=0
    g2: ArcOfCircle CenterX=7.08745 CenterY=-1.11589 CenterZ=0 NormalX=0 NormalY=0 NormalZ=1 AngleXU=0 Radius=1 StartAngle=4.71239 EndAngle=6.28319
    g3: LineSegment StartX=6.08745 StartY=-2.11589 StartZ=0 EndX=7.08745 EndY=-2.11589 EndZ=0
    g4: LineSegment StartX=6.08745 StartY=-4.11588 StartZ=0 EndX=7.08745 EndY=-4.11588 EndZ=0
    g5: ArcOfCircle CenterX=7.08745 CenterY=-1.11589 CenterZ=0 NormalX=0 NormalY=0 NormalZ=1 AngleXU=0 Radius=3 StartAngle=4.71239 EndAngle=6.28319
    g6: ArcOfCircle CenterX=7.08745 CenterY=1.38411 CenterZ=0 NormalX=0 NormalY=0 NormalZ=1 AngleXU=0 Radius=1 StartAngle=5.35e-14 EndAngle=1.5708
    g7: LineSegment StartX=10.0875 StartY=-1.11588 StartZ=0 EndX=10.0875 EndY=1.38411 EndZ=0
    g8: ArcOfCircle CenterX=7.08745 CenterY=1.38411 CenterZ=0 NormalX=0 NormalY=0 NormalZ=1 AngleXU=0 Radius=3 StartAngle=3.57e-14 EndAngle=1.5708
    g9: ArcOfCircle CenterX=4.58745 CenterY=1.38412 CenterZ=0 NormalX=0 NormalY=0 NormalZ=1 AngleXU=0 Radius=1 StartAngle=1.57081 EndAngle=3.14159
    g10: LineSegment StartX=4.58744 StartY=2.38411 StartZ=0 EndX=7.08745 EndY=2.38411 EndZ=0
    g11: LineSegment StartX=4.58745 StartY=4.38411 StartZ=0 EndX=7.08745 EndY=4.38411 EndZ=0
    g12: ArcOfCircle CenterX=4.58745 CenterY=5.38411 CenterZ=0 NormalX=0 NormalY=0 NormalZ=1 AngleXU=0 Radius=1 StartAngle=3.14159 EndAngle=4.71239
    g13: LineSegment StartX=3.58745 StartY=5.38411 StartZ=0 EndX=3.58745 EndY=1.38411 EndZ=0
  constraints (33):
    c: Vertical(g0)
    c: Block(g0)
    c: Block(g1)
    c: Coincident(g2,g1)
    c: Coincident(g3,g0)
    c: Coincident(g3,g2)
    c: Horizontal(g3)
    c: Block(g2)
    c: Coincident(g4,g0)
    c: Horizontal(g4)
    c: Coincident(g5,g2)
    c: Block(g5)
    c: Block(g4)
    c: Coincident(g6,g1)
    c: Block(g6)
    c: Coincident(g7,g5)
    c: Vertical(g7)
    c: Coincident(g8,g6)
    c: Block(g8)
    c: Block(g7)
    c: Coincident(g10,g9)
    c: Coincident(g10,g6)
    c: Horizontal(g10)
    c: Block(g10)
    c: Block(g9)
    c: Coincident(g11,g8)
    c: Horizontal(g11)
    c: Block(g12)
    c: Block(g11)
    c: Coincident(g13,g12)
    c: Coincident(g13,g9)
    c: Vertical(g13)
    c: Tangent(g13,g9)
FEATURE [Part::Extrusion] Extrude039
  Base = -> Sketch044
  Dir = (1,0,0)
  DirMode = 2
  FaceMakerClass = Part::FaceMakerBullseye
  LengthFwd = 10
  LengthRev = 0
  Placement = pos=(8,-22.615,4.115) rot=(0,0,1;3.14159rad)
  Solid = true
  Symmetric = false
FEATURE [App::MeasureDistance] Distance004  label="Distance: 42.16 mm"
  Distance = 42.1607
  P1 = (14.6786,-26.2,1.24491)
  P2 = (-27.4815,-26.2,1.03853)
FEATURE [Sketcher::SketchObject] Sketch045
  FullyConstrained = true
  MapMode = 4
  Placement = pos=(0,0,0) rot=(0.57735,0.57735,0.57735;2.0944rad)
  Support = -> [Cut014]
  sketch-geometry (14):
    g0: LineSegment StartX=6.08745 StartY=-4.11588 StartZ=0 EndX=6.08745 EndY=-2.11589 EndZ=0
    g1: LineSegment StartX=8.08745 StartY=1.38411 StartZ=0 EndX=8.08745 EndY=-1.11589 EndZ=0
    g2: ArcOfCircle CenterX=7.08745 CenterY=-1.11589 CenterZ=0 NormalX=0 NormalY=0 NormalZ=1 AngleXU=0 Radius=1 StartAngle=4.71239 EndAngle=6.28319
    g3: LineSegment StartX=6.08745 StartY=-2.11589 StartZ=0 EndX=7.08745 EndY=-2.11589 EndZ=0
    g4: LineSegment StartX=6.08745 StartY=-4.11588 StartZ=0 EndX=7.08745 EndY=-4.11588 EndZ=0
    g5: ArcOfCircle CenterX=7.08745 CenterY=-1.11589 CenterZ=0 NormalX=0 NormalY=0 NormalZ=1 AngleXU=0 Radius=3 StartAngle=4.71239 EndAngle=6.28319
    g6: ArcOfCircle CenterX=7.08745 CenterY=1.38411 CenterZ=0 NormalX=0 NormalY=0 NormalZ=1 AngleXU=0 Radius=1 StartAngle=5.35e-14 EndAngle=1.5708
    g7: LineSegment StartX=10.0875 StartY=-1.11588 StartZ=0 EndX=10.0875 EndY=1.38411 EndZ=0
    g8: ArcOfCircle CenterX=7.08745 CenterY=1.38411 CenterZ=0 NormalX=0 NormalY=0 NormalZ=1 AngleXU=0 Radius=3 StartAngle=3.57e-14 EndAngle=1.5708
    g9: ArcOfCircle CenterX=4.58745 CenterY=1.38412 CenterZ=0 NormalX=0 NormalY=0 NormalZ=1 AngleXU=0 Radius=1 StartAngle=1.57081 EndAngle=3.14159
    g10: LineSegment StartX=4.58744 StartY=2.38411 StartZ=0 EndX=7.08745 EndY=2.38411 EndZ=0
    g11: LineSegment StartX=4.58745 StartY=4.38411 StartZ=0 EndX=7.08745 EndY=4.38411 EndZ=0
    g12: ArcOfCircle CenterX=4.58745 CenterY=5.38411 CenterZ=0 NormalX=0 NormalY=0 NormalZ=1 AngleXU=0 Radius=1 StartAngle=3.14159 EndAngle=4.71239
    g13: LineSegment StartX=3.58745 StartY=5.38411 StartZ=0 EndX=3.58745 EndY=1.38411 EndZ=0
  constraints (33):
    c: Vertical(g0)
    c: Block(g0)
    c: Block(g1)
    c: Coincident(g2,g1)
    c: Coincident(g3,g0)
    c: Coincident(g3,g2)
    c: Horizontal(g3)
    c: Block(g2)
    c: Coincident(g4,g0)
    c: Horizontal(g4)
    c: Coincident(g5,g2)
    c: Block(g5)
    c: Block(g4)
    c: Coincident(g6,g1)
    c: Block(g6)
    c: Coincident(g7,g5)
    c: Vertical(g7)
    c: Coincident(g8,g6)
    c: Block(g8)
    c: Block(g7)
    c: Coincident(g10,g9)
    c: Coincident(g10,g6)
    c: Horizontal(g10)
    c: Block(g10)
    c: Block(g9)
    c: Coincident(g11,g8)
    c: Horizontal(g11)
    c: Block(g12)
    c: Block(g11)
    c: Coincident(g13,g12)
    c: Coincident(g13,g9)
    c: Vertical(g13)
    c: Tangent(g13,g9)
FEATURE [Part::Extrusion] Extrude040
  Base = -> Sketch045
  Dir = (1,0,0)
  DirMode = 2
  FaceMakerClass = Part::FaceMakerBullseye
  LengthFwd = 10
  LengthRev = 0
  Placement = pos=(-17.5,-22.615,4.115) rot=(0,0,1;3.14159rad)
  Solid = true
  Symmetric = false
FEATURE [Sketcher::SketchObject] Sketch046
  FullyConstrained = true
  MapMode = 4
  Placement = pos=(0,0,0) rot=(0.57735,0.57735,0.57735;2.0944rad)
  Support = -> [Cut014]
  sketch-geometry (14):
    g0: LineSegment StartX=6.08745 StartY=-4.11588 StartZ=0 EndX=6.08745 EndY=-2.11589 EndZ=0
    g1: LineSegment StartX=8.08745 StartY=1.38411 StartZ=0 EndX=8.08745 EndY=-1.11589 EndZ=0
    g2: ArcOfCircle CenterX=7.08745 CenterY=-1.11589 CenterZ=0 NormalX=0 NormalY=0 NormalZ=1 AngleXU=0 Radius=1 StartAngle=4.71239 EndAngle=6.28319
    g3: LineSegment StartX=6.08745 StartY=-2.11589 StartZ=0 EndX=7.08745 EndY=-2.11589 EndZ=0
    g4: LineSegment StartX=6.08745 StartY=-4.11588 StartZ=0 EndX=7.08745 EndY=-4.11588 EndZ=0
    g5: ArcOfCircle CenterX=7.08745 CenterY=-1.11589 CenterZ=0 NormalX=0 NormalY=0 NormalZ=1 AngleXU=0 Radius=3 StartAngle=4.71239 EndAngle=6.28319
    g6: ArcOfCircle CenterX=7.08745 CenterY=1.38411 CenterZ=0 NormalX=0 NormalY=0 NormalZ=1 AngleXU=0 Radius=1 StartAngle=5.35e-14 EndAngle=1.5708
    g7: LineSegment StartX=10.0875 StartY=-1.11588 StartZ=0 EndX=10.0875 EndY=1.38411 EndZ=0
    g8: ArcOfCircle CenterX=7.08745 CenterY=1.38411 CenterZ=0 NormalX=0 NormalY=0 NormalZ=1 AngleXU=0 Radius=3 StartAngle=3.57e-14 EndAngle=1.5708
    g9: ArcOfCircle CenterX=4.58745 CenterY=1.38412 CenterZ=0 NormalX=0 NormalY=0 NormalZ=1 AngleXU=0 Radius=1 StartAngle=1.57081 EndAngle=3.14159
    g10: LineSegment StartX=4.58744 StartY=2.38411 StartZ=0 EndX=7.08745 EndY=2.38411 EndZ=0
    g11: LineSegment StartX=4.58745 StartY=4.38411 StartZ=0 EndX=7.08745 EndY=4.38411 EndZ=0
    g12: ArcOfCircle CenterX=4.58745 CenterY=5.38411 CenterZ=0 NormalX=0 NormalY=0 NormalZ=1 AngleXU=0 Radius=1 StartAngle=3.14159 EndAngle=4.71239
    g13: LineSegment StartX=3.58745 StartY=5.38411 StartZ=0 EndX=3.58745 EndY=1.38411 EndZ=0
  constraints (33):
    c: Vertical(g0)
    c: Block(g0)
    c: Block(g1)
    c: Coincident(g2,g1)
    c: Coincident(g3,g0)
    c: Coincident(g3,g2)
    c: Horizontal(g3)
    c: Block(g2)
    c: Coincident(g4,g0)
    c: Horizontal(g4)
    c: Coincident(g5,g2)
    c: Block(g5)
    c: Block(g4)
    c: Coincident(g6,g1)
    c: Block(g6)
    c: Coincident(g7,g5)
    c: Vertical(g7)
    c: Coincident(g8,g6)
    c: Block(g8)
    c: Block(g7)
    c: Coincident(g10,g9)
    c: Coincident(g10,g6)
    c: Horizontal(g10)
    c: Block(g10)
    c: Block(g9)
    c: Coincident(g11,g8)
    c: Horizontal(g11)
    c: Block(g12)
    c: Block(g11)
    c: Coincident(g13,g12)
    c: Coincident(g13,g9)
    c: Vertical(g13)
    c: Tangent(g13,g9)
FEATURE [Sketcher::SketchObject] Sketch047
  FullyConstrained = true
  MapMode = 4
  Placement = pos=(0,0,0) rot=(0.57735,0.57735,0.57735;2.0944rad)
  Support = -> [Cut014]
  sketch-geometry (14):
    g0: LineSegment StartX=6.08745 StartY=-4.11588 StartZ=0 EndX=6.08745 EndY=-2.11589 EndZ=0
    g1: LineSegment StartX=8.08745 StartY=1.38411 StartZ=0 EndX=8.08745 EndY=-1.11589 EndZ=0
    g2: ArcOfCircle CenterX=7.08745 CenterY=-1.11589 CenterZ=0 NormalX=0 NormalY=0 NormalZ=1 AngleXU=0 Radius=1 StartAngle=4.71239 EndAngle=6.28319
    g3: LineSegment StartX=6.08745 StartY=-2.11589 StartZ=0 EndX=7.08745 EndY=-2.11589 EndZ=0
    g4: LineSegment StartX=6.08745 StartY=-4.11588 StartZ=0 EndX=7.08745 EndY=-4.11588 EndZ=0
    g5: ArcOfCircle CenterX=7.08745 CenterY=-1.11589 CenterZ=0 NormalX=0 NormalY=0 NormalZ=1 AngleXU=0 Radius=3 StartAngle=4.71239 EndAngle=6.28319
    g6: ArcOfCircle CenterX=7.08745 CenterY=1.38411 CenterZ=0 NormalX=0 NormalY=0 NormalZ=1 AngleXU=0 Radius=1 StartAngle=5.35e-14 EndAngle=1.5708
    g7: LineSegment StartX=10.0875 StartY=-1.11588 StartZ=0 EndX=10.0875 EndY=1.38411 EndZ=0
    g8: ArcOfCircle CenterX=7.08745 CenterY=1.38411 CenterZ=0 NormalX=0 NormalY=0 NormalZ=1 AngleXU=0 Radius=3 StartAngle=3.57e-14 EndAngle=1.5708
    g9: ArcOfCircle CenterX=4.58745 CenterY=1.38412 CenterZ=0 NormalX=0 NormalY=0 NormalZ=1 AngleXU=0 Radius=1 StartAngle=1.57081 EndAngle=3.14159
    g10: LineSegment StartX=4.58744 StartY=2.38411 StartZ=0 EndX=7.08745 EndY=2.38411 EndZ=0
    g11: LineSegment StartX=4.58745 StartY=4.38411 StartZ=0 EndX=7.08745 EndY=4.38411 EndZ=0
    g12: ArcOfCircle CenterX=4.58745 CenterY=5.38411 CenterZ=0 NormalX=0 NormalY=0 NormalZ=1 AngleXU=0 Radius=1 StartAngle=3.14159 EndAngle=4.71239
    g13: LineSegment StartX=3.58745 StartY=5.38411 StartZ=0 EndX=3.58745 EndY=1.38411 EndZ=0
  constraints (33):
    c: Vertical(g0)
    c: Block(g0)
    c: Block(g1)
    c: Coincident(g2,g1)
    c: Coincident(g3,g0)
    c: Coincident(g3,g2)
    c: Horizontal(g3)
    c: Block(g2)
    c: Coincident(g4,g0)
    c: Horizontal(g4)
    c: Coincident(g5,g2)
    c: Block(g5)
    c: Block(g4)
    c: Coincident(g6,g1)
    c: Block(g6)
    c: Coincident(g7,g5)
    c: Vertical(g7)
    c: Coincident(g8,g6)
    c: Block(g8)
    c: Block(g7)
    c: Coincident(g10,g9)
    c: Coincident(g10,g6)
    c: Horizontal(g10)
    c: Block(g10)
    c: Block(g9)
    c: Coincident(g11,g8)
    c: Horizontal(g11)
    c: Block(g12)
    c: Block(g11)
    c: Coincident(g13,g12)
    c: Coincident(g13,g9)
    c: Vertical(g13)
    c: Tangent(g13,g9)
FEATURE [Sketcher::SketchObject] Sketch048
  FullyConstrained = true
  MapMode = 4
  Placement = pos=(0,0,0) rot=(0.57735,0.57735,0.57735;2.0944rad)
  Support = -> [Cut014]
  sketch-geometry (14):
    g0: LineSegment StartX=6.08745 StartY=-4.11588 StartZ=0 EndX=6.08745 EndY=-2.11589 EndZ=0
    g1: LineSegment StartX=8.08745 StartY=1.38411 StartZ=0 EndX=8.08745 EndY=-1.11589 EndZ=0
    g2: ArcOfCircle CenterX=7.08745 CenterY=-1.11589 CenterZ=0 NormalX=0 NormalY=0 NormalZ=1 AngleXU=0 Radius=1 StartAngle=4.71239 EndAngle=6.28319
    g3: LineSegment StartX=6.08745 StartY=-2.11589 StartZ=0 EndX=7.08745 EndY=-2.11589 EndZ=0
    g4: LineSegment StartX=6.08745 StartY=-4.11588 StartZ=0 EndX=7.08745 EndY=-4.11588 EndZ=0
    g5: ArcOfCircle CenterX=7.08745 CenterY=-1.11589 CenterZ=0 NormalX=0 NormalY=0 NormalZ=1 AngleXU=0 Radius=3 StartAngle=4.71239 EndAngle=6.28319
    g6: ArcOfCircle CenterX=7.08745 CenterY=1.38411 CenterZ=0 NormalX=0 NormalY=0 NormalZ=1 AngleXU=0 Radius=1 StartAngle=5.35e-14 EndAngle=1.5708
    g7: LineSegment StartX=10.0875 StartY=-1.11588 StartZ=0 EndX=10.0875 EndY=1.38411 EndZ=0
    g8: ArcOfCircle CenterX=7.08745 CenterY=1.38411 CenterZ=0 NormalX=0 NormalY=0 NormalZ=1 AngleXU=0 Radius=3 StartAngle=3.57e-14 EndAngle=1.5708
    g9: ArcOfCircle CenterX=4.58745 CenterY=1.38412 CenterZ=0 NormalX=0 NormalY=0 NormalZ=1 AngleXU=0 Radius=1 StartAngle=1.57081 EndAngle=3.14159
    g10: LineSegment StartX=4.58744 StartY=2.38411 StartZ=0 EndX=7.08745 EndY=2.38411 EndZ=0
    g11: LineSegment StartX=4.58745 StartY=4.38411 StartZ=0 EndX=7.08745 EndY=4.38411 EndZ=0
    g12: ArcOfCircle CenterX=4.58745 CenterY=5.38411 CenterZ=0 NormalX=0 NormalY=0 NormalZ=1 AngleXU=0 Radius=1 StartAngle=3.14159 EndAngle=4.71239
    g13: LineSegment StartX=3.58745 StartY=5.38411 StartZ=0 EndX=3.58745 EndY=1.38411 EndZ=0
  constraints (33):
    c: Vertical(g0)
    c: Block(g0)
    c: Block(g1)
    c: Coincident(g2,g1)
    c: Coincident(g3,g0)
    c: Coincident(g3,g2)
    c: Horizontal(g3)
    c: Block(g2)
    c: Coincident(g4,g0)
    c: Horizontal(g4)
    c: Coincident(g5,g2)
    c: Block(g5)
    c: Block(g4)
    c: Coincident(g6,g1)
    c: Block(g6)
    c: Coincident(g7,g5)
    c: Vertical(g7)
    c: Coincident(g8,g6)
    c: Block(g8)
    c: Block(g7)
    c: Coincident(g10,g9)
    c: Coincident(g10,g6)
    c: Horizontal(g10)
    c: Block(g10)
    c: Block(g9)
    c: Coincident(g11,g8)
    c: Horizontal(g11)
    c: Block(g12)
    c: Block(g11)
    c: Coincident(g13,g12)
    c: Coincident(g13,g9)
    c: Vertical(g13)
    c: Tangent(g13,g9)
FEATURE [Sketcher::SketchObject] Sketch049
  FullyConstrained = true
  MapMode = 4
  Placement = pos=(0,0,0) rot=(0.57735,0.57735,0.57735;2.0944rad)
  Support = -> [Cut014]
  sketch-geometry (14):
    g0: LineSegment StartX=6.08745 StartY=-4.11588 StartZ=0 EndX=6.08745 EndY=-2.11589 EndZ=0
    g1: LineSegment StartX=8.08745 StartY=1.38411 StartZ=0 EndX=8.08745 EndY=-1.11589 EndZ=0
    g2: ArcOfCircle CenterX=7.08745 CenterY=-1.11589 CenterZ=0 NormalX=0 NormalY=0 NormalZ=1 AngleXU=0 Radius=1 StartAngle=4.71239 EndAngle=6.28319
    g3: LineSegment StartX=6.08745 StartY=-2.11589 StartZ=0 EndX=7.08745 EndY=-2.11589 EndZ=0
    g4: LineSegment StartX=6.08745 StartY=-4.11588 StartZ=0 EndX=7.08745 EndY=-4.11588 EndZ=0
    g5: ArcOfCircle CenterX=7.08745 CenterY=-1.11589 CenterZ=0 NormalX=0 NormalY=0 NormalZ=1 AngleXU=0 Radius=3 StartAngle=4.71239 EndAngle=6.28319
    g6: ArcOfCircle CenterX=7.08745 CenterY=1.38411 CenterZ=0 NormalX=0 NormalY=0 NormalZ=1 AngleXU=0 Radius=1 StartAngle=5.35e-14 EndAngle=1.5708
    g7: LineSegment StartX=10.0875 StartY=-1.11588 StartZ=0 EndX=10.0875 EndY=1.38411 EndZ=0
    g8: ArcOfCircle CenterX=7.08745 CenterY=1.38411 CenterZ=0 NormalX=0 NormalY=0 NormalZ=1 AngleXU=0 Radius=3 StartAngle=3.57e-14 EndAngle=1.5708
    g9: ArcOfCircle CenterX=4.58745 CenterY=1.38412 CenterZ=0 NormalX=0 NormalY=0 NormalZ=1 AngleXU=0 Radius=1 StartAngle=1.57081 EndAngle=3.14159
    g10: LineSegment StartX=4.58744 StartY=2.38411 StartZ=0 EndX=7.08745 EndY=2.38411 EndZ=0
    g11: LineSegment StartX=4.58745 StartY=4.38411 StartZ=0 EndX=7.08745 EndY=4.38411 EndZ=0
    g12: ArcOfCircle CenterX=4.58745 CenterY=5.38411 CenterZ=0 NormalX=0 NormalY=0 NormalZ=1 AngleXU=0 Radius=1 StartAngle=3.14159 EndAngle=4.71239
    g13: LineSegment StartX=3.58745 StartY=5.38411 StartZ=0 EndX=3.58745 EndY=1.38411 EndZ=0
  constraints (33):
    c: Vertical(g0)
    c: Block(g0)
    c: Block(g1)
    c: Coincident(g2,g1)
    c: Coincident(g3,g0)
    c: Coincident(g3,g2)
    c: Horizontal(g3)
    c: Block(g2)
    c: Coincident(g4,g0)
    c: Horizontal(g4)
    c: Coincident(g5,g2)
    c: Block(g5)
    c: Block(g4)
    c: Coincident(g6,g1)
    c: Block(g6)
    c: Coincident(g7,g5)
    c: Vertical(g7)
    c: Coincident(g8,g6)
    c: Block(g8)
    c: Block(g7)
    c: Coincident(g10,g9)
    c: Coincident(g10,g6)
    c: Horizontal(g10)
    c: Block(g10)
    c: Block(g9)
    c: Coincident(g11,g8)
    c: Horizontal(g11)
    c: Block(g12)
    c: Block(g11)
    c: Coincident(g13,g12)
    c: Coincident(g13,g9)
    c: Vertical(g13)
    c: Tangent(g13,g9)
FEATURE [Part::Extrusion] Extrude041
  Base = -> Sketch049
  Dir = (1,0,0)
  DirMode = 2
  FaceMakerClass = Part::FaceMakerBullseye
  LengthFwd = 10
  LengthRev = 0
  Placement = pos=(-2,-22.615,14.6) rot=(0,0,1;3.14159rad)
  Solid = true
  Symmetric = false
FEATURE [Part::MultiFuse] Fusion023
  Shapes = -> [Extrude039,Extrude040,Extrude041,Cut014,Fusion015]
FEATURE [Part::Extrusion] Extrude042
  Base = -> Sketch034
  Dir = (0,0.894389,-0.447291)
  DirMode = 2
  FaceMakerClass = Part::FaceMakerBullseye
  LengthFwd = 14
  LengthRev = 0
  Placement = pos=(45.5,-14,11) rot=(1,0,0;0.466003rad)
  Solid = true
  Symmetric = false
FEATURE [Part::Fillet] Fillet021
  Base = -> Extrude042
  Edges = 1 edges r=1.95: [Edge2]
FEATURE [Part::Fillet] Fillet022
  Base = -> Fillet021
  Edges = 1 edges r=1.9: [Edge12]
  Placement = pos=(0,0,0.6) rot=(0,0,1;0rad)
FEATURE [Part::Box] Box014  label="Cube014"
  AttacherType = Attacher::AttachEngine3D
  Height = 2
  Length = 2
  Placement = pos=(-12.85,-28.2,0) rot=(0,0,1;0rad)
  Width = 2
FEATURE [App::MeasureDistance] Distance005  label="Distance: 15.50 mm"
  Distance = 15.5
  P1 = (-17.5,-32.7025,2.99911)
  P2 = (-2,-32.7025,2.99911)
FEATURE [Part::Box] Box015  label="Cube015"
  AttacherType = Attacher::AttachEngine3D
  Height = 2
  Length = 2
  Placement = pos=(-10.85,-28.2,0) rot=(0,0,1;0rad)
  Width = 2
FEATURE [Part::MultiFuse] Fusion024  label="wireHoldersecondery024"
  Placement = pos=(-8.65,0,10.48) rot=(0,0,1;0rad)
  Shapes = -> [Box015,Box014]
FEATURE [App::MeasureDistance] Distance006  label="Distance: 9.44 mm"
  Distance = 9.44274
  P1 = (-8.85,-28.2,0)
  P2 = (-2,-28.1337,6.49911)
FEATURE [Part::Box] Box016  label="Cube016"
  AttacherType = Attacher::AttachEngine3D
  Height = 2
  Length = 2
  Placement = pos=(-12.85,-28.2,0) rot=(0,0,1;0rad)
  Width = 2
FEATURE [Part::Box] Box017  label="Cube017"
  AttacherType = Attacher::AttachEngine3D
  Height = 2
  Length = 2
  Placement = pos=(-10.85,-28.2,0) rot=(0,0,1;0rad)
  Width = 2
FEATURE [Part::MultiFuse] Fusion025  label="wireHoldersecondery025"
  Placement = pos=(1,0,0) rot=(0,0,1;0rad)
  Shapes = -> [Box017,Box016]
FEATURE [App::MeasureDistance] Distance007  label="Distance: 1.58 mm"
  Distance = 1.582
  P1 = (-12,-28.7025,10.4841)
  P2 = (-13.5,-28.2,10.5)
FEATURE [App::MeasureDistance] Distance008  label="Distance: 1.58 mm001"
  Distance = 1.58193
  P1 = (-13.5,-28.2,10.49)
  P2 = (-12,-28.7025,10.4841)
FEATURE [App::MeasureDistance] Distance009  label="Distance: 1.58 mm002"
  Distance = 1.58192
  P1 = (-13.5,-28.2,10.48)
  P2 = (-12,-28.7025,10.4841)
FEATURE [Part::MultiFuse] Fusion026
  Shapes = -> [Fillet022,Fusion025,Fusion024,Fusion023]
